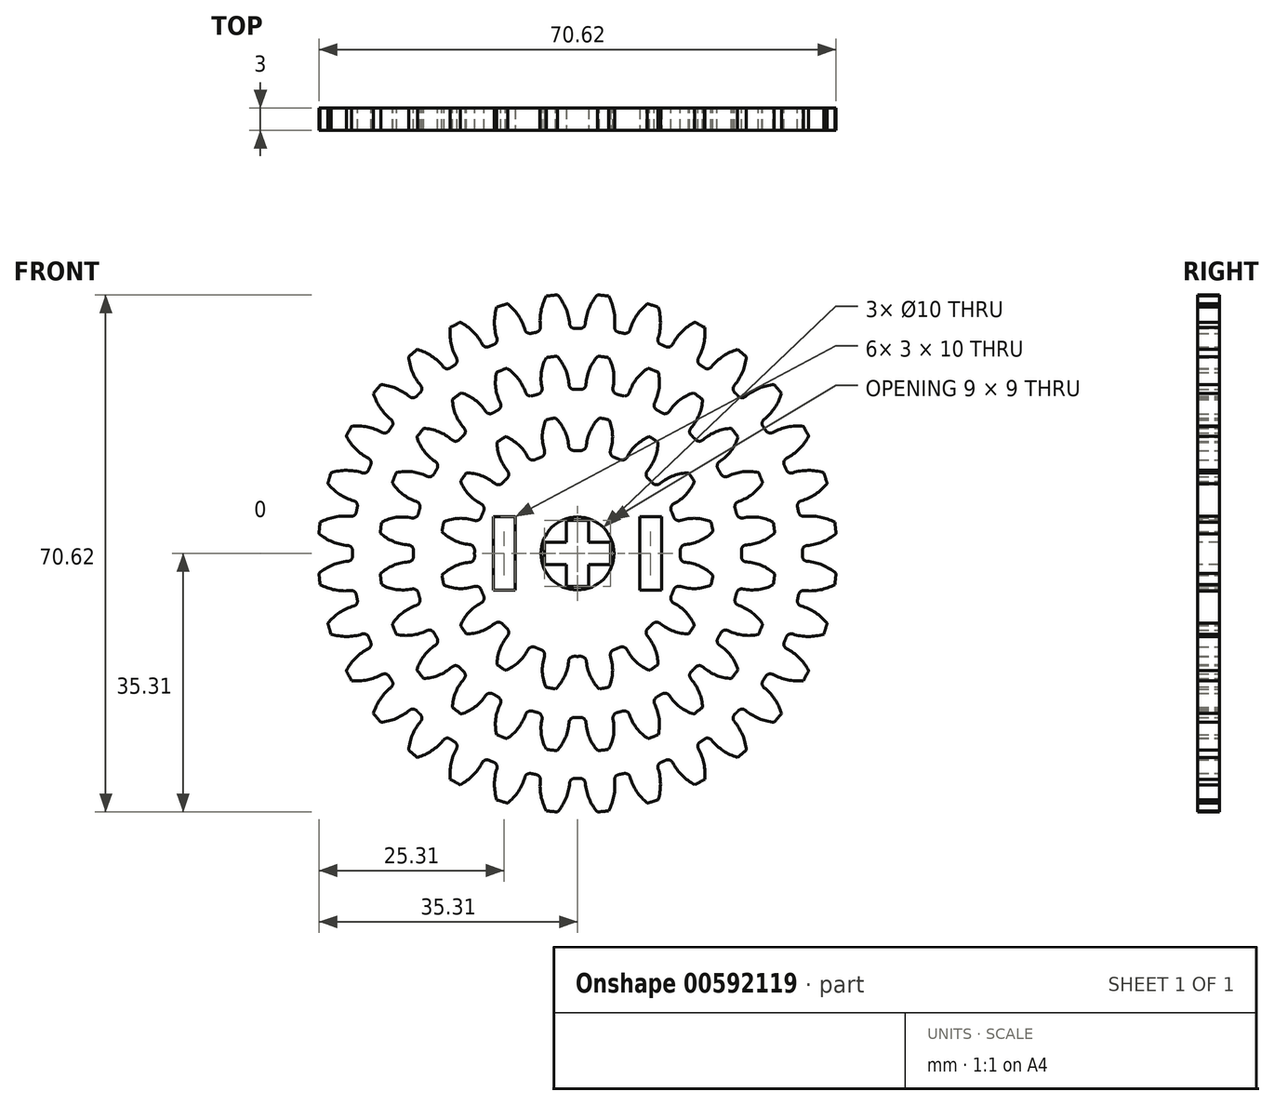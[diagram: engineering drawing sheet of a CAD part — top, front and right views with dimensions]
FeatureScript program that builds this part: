
annotation { "Feature Type Name" : "Feature", "Feature Type Description" : "" }
export const myFeature = defineFeature(function(context is Context, id is Id, definition is map)
    precondition{}
    {
        {
            var Q0;
            Q0=qCreatedBy(makeId("Front.planeOp"),FACE);
            var sketch = newSketch(context, id + "F0", { "sketchPlane" : qUnion([Q0])});
            skArc(sketch, "E0.0", {"start": v(4.27, 26.74) * mm, "mid": v(3.54, 26.85) * mm, "end": v(2.8, 26.94) * mm});
            skArc(sketch, "E1.0", {"start": v(5.4, 21.73) * mm, "mid": v(4.95, 22.07) * mm, "end": v(4.85, 22.62) * mm});
            skArc(sketch, "E2.0", {"start": v(6.18, 21.53) * mm, "mid": v(5.8, 21.63) * mm, "end": v(5.4, 21.73) * mm});
            skArc(sketch, "E3.0", {"start": v(7.1, 22.02) * mm, "mid": v(6.74, 21.58) * mm, "end": v(6.18, 21.53) * mm});
            skPoint(sketch, "E4.0", {"position": v(9.67, 25.3) * mm});
            skArc(sketch, "E5", {"start": v(4.85, 22.62) * mm, "mid": v(4.93, 24.74) * mm, "end": v(4.27, 26.74) * mm});
            skArc(sketch, "E6", {"start": v(7.1, 22.02) * mm, "mid": v(8.1, 23.89) * mm, "end": v(9.67, 25.3) * mm});
            skArc(sketch, "E7.1.0", {"start": v(11.54, 19.2) * mm, "mid": v(11.2, 19.4) * mm, "end": v(10.85, 19.6) * mm});
            skArc(sketch, "E7.1.1", {"start": v(10.85, 19.6) * mm, "mid": v(10.5, 20.03) * mm, "end": v(10.54, 20.6) * mm});
            skPoint(sketch, "E7.1.2", {"position": v(15.9, 21.93) * mm});
            skArc(sketch, "E7.1.3", {"start": v(12.56, 19.43) * mm, "mid": v(12.1, 19.1) * mm, "end": v(11.54, 19.2) * mm});
            skArc(sketch, "E7.1.4", {"start": v(12.56, 19.43) * mm, "mid": v(14, 20.98) * mm, "end": v(15.9, 21.93) * mm});
            skArc(sketch, "E7.1.5", {"start": v(10.54, 20.6) * mm, "mid": v(11.16, 22.62) * mm, "end": v(11.05, 24.73) * mm});
            skArc(sketch, "E7.1.6", {"start": v(11.05, 24.73) * mm, "mid": v(10.36, 25.02) * mm, "end": v(9.67, 25.3) * mm});
            skArc(sketch, "E7.2.0", {"start": v(16.12, 15.55) * mm, "mid": v(15.84, 15.84) * mm, "end": v(15.55, 16.12) * mm});
            skArc(sketch, "E7.2.1", {"start": v(15.55, 16.12) * mm, "mid": v(15.32, 16.63) * mm, "end": v(15.52, 17.16) * mm});
            skPoint(sketch, "E7.2.2", {"position": v(21.03, 17.07) * mm});
            skArc(sketch, "E7.2.3", {"start": v(17.16, 15.52) * mm, "mid": v(16.63, 15.32) * mm, "end": v(16.12, 15.55) * mm});
            skArc(sketch, "E7.2.4", {"start": v(17.16, 15.52) * mm, "mid": v(18.96, 16.64) * mm, "end": v(21.03, 17.07) * mm});
            skArc(sketch, "E7.2.5", {"start": v(15.52, 17.16) * mm, "mid": v(16.64, 18.96) * mm, "end": v(17.07, 21.03) * mm});
            skArc(sketch, "E7.2.6", {"start": v(17.07, 21.03) * mm, "mid": v(16.49, 21.49) * mm, "end": v(15.9, 21.93) * mm});
            skArc(sketch, "E7.3.0", {"start": v(19.6, 10.85) * mm, "mid": v(19.4, 11.2) * mm, "end": v(19.2, 11.54) * mm});
            skArc(sketch, "E7.3.1", {"start": v(19.2, 11.54) * mm, "mid": v(19.1, 12.1) * mm, "end": v(19.43, 12.56) * mm});
            skPoint(sketch, "E7.3.2", {"position": v(24.73, 11.05) * mm});
            skArc(sketch, "E7.3.3", {"start": v(20.6, 10.54) * mm, "mid": v(20.03, 10.5) * mm, "end": v(19.6, 10.85) * mm});
            skArc(sketch, "E7.3.4", {"start": v(20.6, 10.54) * mm, "mid": v(22.62, 11.16) * mm, "end": v(24.73, 11.05) * mm});
            skArc(sketch, "E7.3.5", {"start": v(19.43, 12.56) * mm, "mid": v(20.98, 14) * mm, "end": v(21.93, 15.9) * mm});
            skArc(sketch, "E7.3.6", {"start": v(21.93, 15.9) * mm, "mid": v(21.49, 16.49) * mm, "end": v(21.03, 17.07) * mm});
            skArc(sketch, "E7.4.0", {"start": v(21.73, 5.4) * mm, "mid": v(21.63, 5.8) * mm, "end": v(21.53, 6.18) * mm});
            skArc(sketch, "E7.4.1", {"start": v(21.53, 6.18) * mm, "mid": v(21.58, 6.74) * mm, "end": v(22.02, 7.1) * mm});
            skPoint(sketch, "E7.4.2", {"position": v(26.74, 4.27) * mm});
            skArc(sketch, "E7.4.3", {"start": v(22.62, 4.85) * mm, "mid": v(22.07, 4.95) * mm, "end": v(21.73, 5.4) * mm});
            skArc(sketch, "E7.4.4", {"start": v(22.62, 4.85) * mm, "mid": v(24.74, 4.93) * mm, "end": v(26.74, 4.27) * mm});
            skArc(sketch, "E7.4.5", {"start": v(22.02, 7.1) * mm, "mid": v(23.89, 8.1) * mm, "end": v(25.3, 9.67) * mm});
            skArc(sketch, "E7.4.6", {"start": v(25.3, 9.67) * mm, "mid": v(25.02, 10.36) * mm, "end": v(24.73, 11.05) * mm});
            skArc(sketch, "E7.5.0", {"start": v(22.4, -0.4) * mm, "mid": v(22.4, 0) * mm, "end": v(22.4, 0.4) * mm});
            skArc(sketch, "E7.5.1", {"start": v(22.4, 0.4) * mm, "mid": v(22.6, 0.93) * mm, "end": v(23.1, 1.17) * mm});
            skPoint(sketch, "E7.5.2", {"position": v(26.94, -2.8) * mm});
            skArc(sketch, "E7.5.3", {"start": v(23.1, -1.17) * mm, "mid": v(22.6, -0.93) * mm, "end": v(22.4, -0.4) * mm});
            skArc(sketch, "E7.5.4", {"start": v(23.1, -1.17) * mm, "mid": v(25.17, -1.64) * mm, "end": v(26.94, -2.8) * mm});
            skArc(sketch, "E7.5.5", {"start": v(23.1, 1.17) * mm, "mid": v(25.17, 1.64) * mm, "end": v(26.94, 2.8) * mm});
            skArc(sketch, "E7.5.6", {"start": v(26.94, 2.8) * mm, "mid": v(26.85, 3.54) * mm, "end": v(26.74, 4.27) * mm});
            skArc(sketch, "E7.6.0", {"start": v(21.53, -6.18) * mm, "mid": v(21.63, -5.8) * mm, "end": v(21.73, -5.4) * mm});
            skArc(sketch, "E7.6.1", {"start": v(21.73, -5.4) * mm, "mid": v(22.07, -4.95) * mm, "end": v(22.62, -4.85) * mm});
            skPoint(sketch, "E7.6.2", {"position": v(25.3, -9.67) * mm});
            skArc(sketch, "E7.6.3", {"start": v(22.02, -7.1) * mm, "mid": v(21.58, -6.74) * mm, "end": v(21.53, -6.18) * mm});
            skArc(sketch, "E7.6.4", {"start": v(22.02, -7.1) * mm, "mid": v(23.89, -8.1) * mm, "end": v(25.3, -9.67) * mm});
            skArc(sketch, "E7.6.5", {"start": v(22.62, -4.85) * mm, "mid": v(24.74, -4.93) * mm, "end": v(26.74, -4.27) * mm});
            skArc(sketch, "E7.6.6", {"start": v(26.74, -4.27) * mm, "mid": v(26.85, -3.54) * mm, "end": v(26.94, -2.8) * mm});
            skArc(sketch, "E7.7.0", {"start": v(19.2, -11.54) * mm, "mid": v(19.4, -11.2) * mm, "end": v(19.6, -10.85) * mm});
            skArc(sketch, "E7.7.1", {"start": v(19.6, -10.85) * mm, "mid": v(20.03, -10.5) * mm, "end": v(20.6, -10.54) * mm});
            skPoint(sketch, "E7.7.2", {"position": v(21.93, -15.9) * mm});
            skArc(sketch, "E7.7.3", {"start": v(19.43, -12.56) * mm, "mid": v(19.1, -12.1) * mm, "end": v(19.2, -11.54) * mm});
            skArc(sketch, "E7.7.4", {"start": v(19.43, -12.56) * mm, "mid": v(20.98, -14) * mm, "end": v(21.93, -15.9) * mm});
            skArc(sketch, "E7.7.5", {"start": v(20.6, -10.54) * mm, "mid": v(22.62, -11.16) * mm, "end": v(24.73, -11.05) * mm});
            skArc(sketch, "E7.7.6", {"start": v(24.73, -11.05) * mm, "mid": v(25.02, -10.36) * mm, "end": v(25.3, -9.67) * mm});
            skArc(sketch, "E7.8.0", {"start": v(15.55, -16.12) * mm, "mid": v(15.84, -15.84) * mm, "end": v(16.12, -15.55) * mm});
            skArc(sketch, "E7.8.1", {"start": v(16.12, -15.55) * mm, "mid": v(16.63, -15.32) * mm, "end": v(17.16, -15.52) * mm});
            skPoint(sketch, "E7.8.2", {"position": v(17.07, -21.03) * mm});
            skArc(sketch, "E7.8.3", {"start": v(15.52, -17.16) * mm, "mid": v(15.32, -16.63) * mm, "end": v(15.55, -16.12) * mm});
            skArc(sketch, "E7.8.4", {"start": v(15.52, -17.16) * mm, "mid": v(16.64, -18.96) * mm, "end": v(17.07, -21.03) * mm});
            skArc(sketch, "E7.8.5", {"start": v(17.16, -15.52) * mm, "mid": v(18.96, -16.64) * mm, "end": v(21.03, -17.07) * mm});
            skArc(sketch, "E7.8.6", {"start": v(21.03, -17.07) * mm, "mid": v(21.49, -16.49) * mm, "end": v(21.93, -15.9) * mm});
            skArc(sketch, "E7.9.0", {"start": v(10.85, -19.6) * mm, "mid": v(11.2, -19.4) * mm, "end": v(11.54, -19.2) * mm});
            skArc(sketch, "E7.9.1", {"start": v(11.54, -19.2) * mm, "mid": v(12.1, -19.1) * mm, "end": v(12.56, -19.43) * mm});
            skPoint(sketch, "E7.9.2", {"position": v(11.05, -24.73) * mm});
            skArc(sketch, "E7.9.3", {"start": v(10.54, -20.6) * mm, "mid": v(10.5, -20.03) * mm, "end": v(10.85, -19.6) * mm});
            skArc(sketch, "E7.9.4", {"start": v(10.54, -20.6) * mm, "mid": v(11.16, -22.62) * mm, "end": v(11.05, -24.73) * mm});
            skArc(sketch, "E7.9.5", {"start": v(12.56, -19.43) * mm, "mid": v(14, -20.98) * mm, "end": v(15.9, -21.93) * mm});
            skArc(sketch, "E7.9.6", {"start": v(15.9, -21.93) * mm, "mid": v(16.49, -21.49) * mm, "end": v(17.07, -21.03) * mm});
            skArc(sketch, "E7.10.0", {"start": v(5.4, -21.73) * mm, "mid": v(5.8, -21.63) * mm, "end": v(6.18, -21.53) * mm});
            skArc(sketch, "E7.10.1", {"start": v(6.18, -21.53) * mm, "mid": v(6.74, -21.58) * mm, "end": v(7.1, -22.02) * mm});
            skPoint(sketch, "E7.10.2", {"position": v(4.27, -26.74) * mm});
            skArc(sketch, "E7.10.3", {"start": v(4.85, -22.62) * mm, "mid": v(4.95, -22.07) * mm, "end": v(5.4, -21.73) * mm});
            skArc(sketch, "E7.10.4", {"start": v(4.85, -22.62) * mm, "mid": v(4.93, -24.74) * mm, "end": v(4.27, -26.74) * mm});
            skArc(sketch, "E7.10.5", {"start": v(7.1, -22.02) * mm, "mid": v(8.1, -23.89) * mm, "end": v(9.67, -25.3) * mm});
            skArc(sketch, "E7.10.6", {"start": v(9.67, -25.3) * mm, "mid": v(10.36, -25.02) * mm, "end": v(11.05, -24.73) * mm});
            skArc(sketch, "E7.11.0", {"start": v(-0.4, -22.4) * mm, "mid": v(0, -22.4) * mm, "end": v(0.4, -22.4) * mm});
            skArc(sketch, "E7.11.1", {"start": v(0.4, -22.4) * mm, "mid": v(0.93, -22.6) * mm, "end": v(1.17, -23.1) * mm});
            skPoint(sketch, "E7.11.2", {"position": v(-2.8, -26.94) * mm});
            skArc(sketch, "E7.11.3", {"start": v(-1.17, -23.1) * mm, "mid": v(-0.93, -22.6) * mm, "end": v(-0.4, -22.4) * mm});
            skArc(sketch, "E7.11.4", {"start": v(-1.17, -23.1) * mm, "mid": v(-1.64, -25.17) * mm, "end": v(-2.8, -26.94) * mm});
            skArc(sketch, "E7.11.5", {"start": v(1.17, -23.1) * mm, "mid": v(1.64, -25.17) * mm, "end": v(2.8, -26.94) * mm});
            skArc(sketch, "E7.11.6", {"start": v(2.8, -26.94) * mm, "mid": v(3.54, -26.85) * mm, "end": v(4.27, -26.74) * mm});
            skArc(sketch, "E7.12.0", {"start": v(-6.18, -21.53) * mm, "mid": v(-5.8, -21.63) * mm, "end": v(-5.4, -21.73) * mm});
            skArc(sketch, "E7.12.1", {"start": v(-5.4, -21.73) * mm, "mid": v(-4.95, -22.07) * mm, "end": v(-4.85, -22.62) * mm});
            skPoint(sketch, "E7.12.2", {"position": v(-9.67, -25.3) * mm});
            skArc(sketch, "E7.12.3", {"start": v(-7.1, -22.02) * mm, "mid": v(-6.74, -21.58) * mm, "end": v(-6.18, -21.53) * mm});
            skArc(sketch, "E7.12.4", {"start": v(-7.1, -22.02) * mm, "mid": v(-8.1, -23.89) * mm, "end": v(-9.67, -25.3) * mm});
            skArc(sketch, "E7.12.5", {"start": v(-4.85, -22.62) * mm, "mid": v(-4.93, -24.74) * mm, "end": v(-4.27, -26.74) * mm});
            skArc(sketch, "E7.12.6", {"start": v(-4.27, -26.74) * mm, "mid": v(-3.54, -26.85) * mm, "end": v(-2.8, -26.94) * mm});
            skArc(sketch, "E7.13.0", {"start": v(-11.54, -19.2) * mm, "mid": v(-11.2, -19.4) * mm, "end": v(-10.85, -19.6) * mm});
            skArc(sketch, "E7.13.1", {"start": v(-10.85, -19.6) * mm, "mid": v(-10.5, -20.03) * mm, "end": v(-10.54, -20.6) * mm});
            skPoint(sketch, "E7.13.2", {"position": v(-15.9, -21.93) * mm});
            skArc(sketch, "E7.13.3", {"start": v(-12.56, -19.43) * mm, "mid": v(-12.1, -19.1) * mm, "end": v(-11.54, -19.2) * mm});
            skArc(sketch, "E7.13.4", {"start": v(-12.56, -19.43) * mm, "mid": v(-14, -20.98) * mm, "end": v(-15.9, -21.93) * mm});
            skArc(sketch, "E7.13.5", {"start": v(-10.54, -20.6) * mm, "mid": v(-11.16, -22.62) * mm, "end": v(-11.05, -24.73) * mm});
            skArc(sketch, "E7.13.6", {"start": v(-11.05, -24.73) * mm, "mid": v(-10.36, -25.02) * mm, "end": v(-9.67, -25.3) * mm});
            skArc(sketch, "E7.14.0", {"start": v(-16.12, -15.55) * mm, "mid": v(-15.84, -15.84) * mm, "end": v(-15.55, -16.12) * mm});
            skArc(sketch, "E7.14.1", {"start": v(-15.55, -16.12) * mm, "mid": v(-15.32, -16.63) * mm, "end": v(-15.52, -17.16) * mm});
            skPoint(sketch, "E7.14.2", {"position": v(-21.03, -17.07) * mm});
            skArc(sketch, "E7.14.3", {"start": v(-17.16, -15.52) * mm, "mid": v(-16.63, -15.32) * mm, "end": v(-16.12, -15.55) * mm});
            skArc(sketch, "E7.14.4", {"start": v(-17.16, -15.52) * mm, "mid": v(-18.96, -16.64) * mm, "end": v(-21.03, -17.07) * mm});
            skArc(sketch, "E7.14.5", {"start": v(-15.52, -17.16) * mm, "mid": v(-16.64, -18.96) * mm, "end": v(-17.07, -21.03) * mm});
            skArc(sketch, "E7.14.6", {"start": v(-17.07, -21.03) * mm, "mid": v(-16.49, -21.49) * mm, "end": v(-15.9, -21.93) * mm});
            skArc(sketch, "E7.15.0", {"start": v(-19.6, -10.85) * mm, "mid": v(-19.4, -11.2) * mm, "end": v(-19.2, -11.54) * mm});
            skArc(sketch, "E7.15.1", {"start": v(-19.2, -11.54) * mm, "mid": v(-19.1, -12.1) * mm, "end": v(-19.43, -12.56) * mm});
            skPoint(sketch, "E7.15.2", {"position": v(-24.73, -11.05) * mm});
            skArc(sketch, "E7.15.3", {"start": v(-20.6, -10.54) * mm, "mid": v(-20.03, -10.5) * mm, "end": v(-19.6, -10.85) * mm});
            skArc(sketch, "E7.15.4", {"start": v(-20.6, -10.54) * mm, "mid": v(-22.62, -11.16) * mm, "end": v(-24.73, -11.05) * mm});
            skArc(sketch, "E7.15.5", {"start": v(-19.43, -12.56) * mm, "mid": v(-20.98, -14) * mm, "end": v(-21.93, -15.9) * mm});
            skArc(sketch, "E7.15.6", {"start": v(-21.93, -15.9) * mm, "mid": v(-21.49, -16.49) * mm, "end": v(-21.03, -17.07) * mm});
            skArc(sketch, "E7.16.0", {"start": v(-21.73, -5.4) * mm, "mid": v(-21.63, -5.8) * mm, "end": v(-21.53, -6.18) * mm});
            skArc(sketch, "E7.16.1", {"start": v(-21.53, -6.18) * mm, "mid": v(-21.58, -6.74) * mm, "end": v(-22.02, -7.1) * mm});
            skPoint(sketch, "E7.16.2", {"position": v(-26.74, -4.27) * mm});
            skArc(sketch, "E7.16.3", {"start": v(-22.62, -4.85) * mm, "mid": v(-22.07, -4.95) * mm, "end": v(-21.73, -5.4) * mm});
            skArc(sketch, "E7.16.4", {"start": v(-22.62, -4.85) * mm, "mid": v(-24.74, -4.93) * mm, "end": v(-26.74, -4.27) * mm});
            skArc(sketch, "E7.16.5", {"start": v(-22.02, -7.1) * mm, "mid": v(-23.89, -8.1) * mm, "end": v(-25.3, -9.67) * mm});
            skArc(sketch, "E7.16.6", {"start": v(-25.3, -9.67) * mm, "mid": v(-25.02, -10.36) * mm, "end": v(-24.73, -11.05) * mm});
            skArc(sketch, "E7.17.0", {"start": v(-22.4, 0.4) * mm, "mid": v(-22.4, 0) * mm, "end": v(-22.4, -0.4) * mm});
            skArc(sketch, "E7.17.1", {"start": v(-22.4, -0.4) * mm, "mid": v(-22.6, -0.93) * mm, "end": v(-23.1, -1.17) * mm});
            skPoint(sketch, "E7.17.2", {"position": v(-26.94, 2.8) * mm});
            skArc(sketch, "E7.17.3", {"start": v(-23.1, 1.17) * mm, "mid": v(-22.6, 0.93) * mm, "end": v(-22.4, 0.4) * mm});
            skArc(sketch, "E7.17.4", {"start": v(-23.1, 1.17) * mm, "mid": v(-25.17, 1.64) * mm, "end": v(-26.94, 2.8) * mm});
            skArc(sketch, "E7.17.5", {"start": v(-23.1, -1.17) * mm, "mid": v(-25.17, -1.64) * mm, "end": v(-26.94, -2.8) * mm});
            skArc(sketch, "E7.17.6", {"start": v(-26.94, -2.8) * mm, "mid": v(-26.85, -3.54) * mm, "end": v(-26.74, -4.27) * mm});
            skArc(sketch, "E7.18.0", {"start": v(-21.53, 6.18) * mm, "mid": v(-21.63, 5.8) * mm, "end": v(-21.73, 5.4) * mm});
            skArc(sketch, "E7.18.1", {"start": v(-21.73, 5.4) * mm, "mid": v(-22.07, 4.95) * mm, "end": v(-22.62, 4.85) * mm});
            skPoint(sketch, "E7.18.2", {"position": v(-25.3, 9.67) * mm});
            skArc(sketch, "E7.18.3", {"start": v(-22.02, 7.1) * mm, "mid": v(-21.58, 6.74) * mm, "end": v(-21.53, 6.18) * mm});
            skArc(sketch, "E7.18.4", {"start": v(-22.02, 7.1) * mm, "mid": v(-23.89, 8.1) * mm, "end": v(-25.3, 9.67) * mm});
            skArc(sketch, "E7.18.5", {"start": v(-22.62, 4.85) * mm, "mid": v(-24.74, 4.93) * mm, "end": v(-26.74, 4.27) * mm});
            skArc(sketch, "E7.18.6", {"start": v(-26.74, 4.27) * mm, "mid": v(-26.85, 3.54) * mm, "end": v(-26.94, 2.8) * mm});
            skArc(sketch, "E7.19.0", {"start": v(-19.2, 11.54) * mm, "mid": v(-19.4, 11.2) * mm, "end": v(-19.6, 10.85) * mm});
            skArc(sketch, "E7.19.1", {"start": v(-19.6, 10.85) * mm, "mid": v(-20.03, 10.5) * mm, "end": v(-20.6, 10.54) * mm});
            skPoint(sketch, "E7.19.2", {"position": v(-21.93, 15.9) * mm});
            skArc(sketch, "E7.19.3", {"start": v(-19.43, 12.56) * mm, "mid": v(-19.1, 12.1) * mm, "end": v(-19.2, 11.54) * mm});
            skArc(sketch, "E7.19.4", {"start": v(-19.43, 12.56) * mm, "mid": v(-20.98, 14) * mm, "end": v(-21.93, 15.9) * mm});
            skArc(sketch, "E7.19.5", {"start": v(-20.6, 10.54) * mm, "mid": v(-22.62, 11.16) * mm, "end": v(-24.73, 11.05) * mm});
            skArc(sketch, "E7.19.6", {"start": v(-24.73, 11.05) * mm, "mid": v(-25.02, 10.36) * mm, "end": v(-25.3, 9.67) * mm});
            skArc(sketch, "E7.20.0", {"start": v(-15.55, 16.12) * mm, "mid": v(-15.84, 15.84) * mm, "end": v(-16.12, 15.55) * mm});
            skArc(sketch, "E7.20.1", {"start": v(-16.12, 15.55) * mm, "mid": v(-16.63, 15.32) * mm, "end": v(-17.16, 15.52) * mm});
            skPoint(sketch, "E7.20.2", {"position": v(-17.07, 21.03) * mm});
            skArc(sketch, "E7.20.3", {"start": v(-15.52, 17.16) * mm, "mid": v(-15.32, 16.63) * mm, "end": v(-15.55, 16.12) * mm});
            skArc(sketch, "E7.20.4", {"start": v(-15.52, 17.16) * mm, "mid": v(-16.64, 18.96) * mm, "end": v(-17.07, 21.03) * mm});
            skArc(sketch, "E7.20.5", {"start": v(-17.16, 15.52) * mm, "mid": v(-18.96, 16.64) * mm, "end": v(-21.03, 17.07) * mm});
            skArc(sketch, "E7.20.6", {"start": v(-21.03, 17.07) * mm, "mid": v(-21.49, 16.49) * mm, "end": v(-21.93, 15.9) * mm});
            skArc(sketch, "E7.21.0", {"start": v(-10.85, 19.6) * mm, "mid": v(-11.2, 19.4) * mm, "end": v(-11.54, 19.2) * mm});
            skArc(sketch, "E7.21.1", {"start": v(-11.54, 19.2) * mm, "mid": v(-12.1, 19.1) * mm, "end": v(-12.56, 19.43) * mm});
            skPoint(sketch, "E7.21.2", {"position": v(-11.05, 24.73) * mm});
            skArc(sketch, "E7.21.3", {"start": v(-10.54, 20.6) * mm, "mid": v(-10.5, 20.03) * mm, "end": v(-10.85, 19.6) * mm});
            skArc(sketch, "E7.21.4", {"start": v(-10.54, 20.6) * mm, "mid": v(-11.16, 22.62) * mm, "end": v(-11.05, 24.73) * mm});
            skArc(sketch, "E7.21.5", {"start": v(-12.56, 19.43) * mm, "mid": v(-14, 20.98) * mm, "end": v(-15.9, 21.93) * mm});
            skArc(sketch, "E7.21.6", {"start": v(-15.9, 21.93) * mm, "mid": v(-16.49, 21.49) * mm, "end": v(-17.07, 21.03) * mm});
            skArc(sketch, "E7.22.0", {"start": v(-5.4, 21.73) * mm, "mid": v(-5.8, 21.63) * mm, "end": v(-6.18, 21.53) * mm});
            skArc(sketch, "E7.22.1", {"start": v(-6.18, 21.53) * mm, "mid": v(-6.74, 21.58) * mm, "end": v(-7.1, 22.02) * mm});
            skPoint(sketch, "E7.22.2", {"position": v(-4.27, 26.74) * mm});
            skArc(sketch, "E7.22.3", {"start": v(-4.85, 22.62) * mm, "mid": v(-4.95, 22.07) * mm, "end": v(-5.4, 21.73) * mm});
            skArc(sketch, "E7.22.4", {"start": v(-4.85, 22.62) * mm, "mid": v(-4.93, 24.74) * mm, "end": v(-4.27, 26.74) * mm});
            skArc(sketch, "E7.22.5", {"start": v(-7.1, 22.02) * mm, "mid": v(-8.1, 23.89) * mm, "end": v(-9.67, 25.3) * mm});
            skArc(sketch, "E7.22.6", {"start": v(-9.67, 25.3) * mm, "mid": v(-10.36, 25.02) * mm, "end": v(-11.05, 24.73) * mm});
            skArc(sketch, "E7.23.0", {"start": v(0.4, 22.4) * mm, "mid": v(0, 22.4) * mm, "end": v(-0.4, 22.4) * mm});
            skArc(sketch, "E7.23.1", {"start": v(-0.4, 22.4) * mm, "mid": v(-0.93, 22.6) * mm, "end": v(-1.17, 23.1) * mm});
            skPoint(sketch, "E7.23.2", {"position": v(2.8, 26.94) * mm});
            skArc(sketch, "E7.23.3", {"start": v(1.17, 23.1) * mm, "mid": v(0.93, 22.6) * mm, "end": v(0.4, 22.4) * mm});
            skArc(sketch, "E7.23.4", {"start": v(1.17, 23.1) * mm, "mid": v(1.64, 25.17) * mm, "end": v(2.8, 26.94) * mm});
            skArc(sketch, "E7.23.5", {"start": v(-1.17, 23.1) * mm, "mid": v(-1.64, 25.17) * mm, "end": v(-2.8, 26.94) * mm});
            skArc(sketch, "E7.23.6", {"start": v(-2.8, 26.94) * mm, "mid": v(-3.54, 26.85) * mm, "end": v(-4.27, 26.74) * mm});
            skLineSegment(sketch, "E7.anchor1", {"start": v(0, 0) * mm, "end": v(-1.06, 23.89) * mm, "construction": true});
            skLineSegment(sketch, "E7.anchor2", {"start": v(0, 0) * mm, "end": v(-7.2, 22.8) * mm, "construction": true});
            skLineSegment(sketch, "E8.bottom", {"start": v(1.38, 1.37) * mm, "end": v(-1.37, 1.37) * mm});
            skLineSegment(sketch, "E8.top", {"start": v(1.37, -1.38) * mm, "end": v(-1.37, -1.38) * mm});
            skLineSegment(sketch, "E8.left", {"start": v(1.37, 1.37) * mm, "end": v(1.37, -1.38) * mm});
            skLineSegment(sketch, "E8.right", {"start": v(-1.37, 1.38) * mm, "end": v(-1.37, -1.37) * mm});
            skSolve(sketch);
        }
        {
            var Q0;
            Q0=makeQuery(id+"F0.imprint","IMPRINT",FACE,{"disambiguationData":[TD([[makeQuery(id+"F0.imprint","IMPRINT",EDGE,{"derivedFrom":sQuery(id+"F0.wireOp",EDGE,"E0.0")}),1.0]])]});
            extrude(context, id + "F1", {"entities" : qUnion([Q0]), "depth" : 3 * mm, "offsetDistance" : 25 * mm});
        }
        {
            var Q0;
            Q0=qCreatedBy(makeId("Front.planeOp"),FACE);
            var sketch = newSketch(context, id + "F2", { "sketchPlane" : qUnion([Q0])});
            skArc(sketch, "E9.0", {"start": v(4.33, 18.24) * mm, "mid": v(3.66, 18.39) * mm, "end": v(2.98, 18.51) * mm});
            skArc(sketch, "E10.0", {"start": v(4.98, 13.15) * mm, "mid": v(4.56, 13.54) * mm, "end": v(4.52, 14.12) * mm});
            skArc(sketch, "E11.0", {"start": v(5.78, 12.82) * mm, "mid": v(5.38, 13) * mm, "end": v(4.98, 13.15) * mm});
            skArc(sketch, "E12.0", {"start": v(6.79, 13.18) * mm, "mid": v(6.35, 12.8) * mm, "end": v(5.78, 12.82) * mm});
            skPoint(sketch, "E13.0", {"position": v(9.83, 15.96) * mm});
            skArc(sketch, "E14", {"start": v(4.52, 14.12) * mm, "mid": v(4.8, 16.2) * mm, "end": v(4.33, 18.24) * mm});
            skArc(sketch, "E15", {"start": v(6.79, 13.18) * mm, "mid": v(8.06, 14.84) * mm, "end": v(9.83, 15.96) * mm});
            skArc(sketch, "E16.1.0", {"start": v(11.31, 9.57) * mm, "mid": v(10.77, 9.4) * mm, "end": v(10.24, 9.63) * mm});
            skArc(sketch, "E16.1.1", {"start": v(10.24, 9.63) * mm, "mid": v(9.94, 9.94) * mm, "end": v(9.63, 10.24) * mm});
            skArc(sketch, "E16.1.2", {"start": v(9.57, 11.31) * mm, "mid": v(10.63, 13.13) * mm, "end": v(10.98, 15.2) * mm});
            skArc(sketch, "E16.1.3", {"start": v(11.31, 9.57) * mm, "mid": v(13.13, 10.63) * mm, "end": v(15.2, 10.98) * mm});
            skArc(sketch, "E16.1.4", {"start": v(10.98, 15.2) * mm, "mid": v(10.42, 15.59) * mm, "end": v(9.83, 15.96) * mm});
            skArc(sketch, "E16.1.5", {"start": v(9.63, 10.24) * mm, "mid": v(9.4, 10.77) * mm, "end": v(9.57, 11.31) * mm});
            skPoint(sketch, "E16.1.6", {"position": v(15.2, 10.98) * mm});
            skArc(sketch, "E16.2.0", {"start": v(14.12, 4.52) * mm, "mid": v(13.54, 4.56) * mm, "end": v(13.15, 4.98) * mm});
            skArc(sketch, "E16.2.1", {"start": v(13.15, 4.98) * mm, "mid": v(13, 5.38) * mm, "end": v(12.82, 5.78) * mm});
            skArc(sketch, "E16.2.2", {"start": v(13.18, 6.79) * mm, "mid": v(14.84, 8.06) * mm, "end": v(15.96, 9.83) * mm});
            skArc(sketch, "E16.2.3", {"start": v(14.12, 4.52) * mm, "mid": v(16.2, 4.8) * mm, "end": v(18.24, 4.33) * mm});
            skArc(sketch, "E16.2.4", {"start": v(15.96, 9.83) * mm, "mid": v(15.59, 10.42) * mm, "end": v(15.2, 10.98) * mm});
            skArc(sketch, "E16.2.5", {"start": v(12.82, 5.78) * mm, "mid": v(12.8, 6.35) * mm, "end": v(13.18, 6.79) * mm});
            skPoint(sketch, "E16.2.6", {"position": v(18.24, 4.33) * mm});
            skArc(sketch, "E16.3.0", {"start": v(14.77, -1.23) * mm, "mid": v(14.25, -0.97) * mm, "end": v(14.05, -0.43) * mm});
            skArc(sketch, "E16.3.1", {"start": v(14.05, -0.43) * mm, "mid": v(14.06, 0) * mm, "end": v(14.05, 0.43) * mm});
            skArc(sketch, "E16.3.2", {"start": v(14.77, 1.23) * mm, "mid": v(16.8, 1.77) * mm, "end": v(18.51, 2.98) * mm});
            skArc(sketch, "E16.3.3", {"start": v(14.77, -1.23) * mm, "mid": v(16.8, -1.77) * mm, "end": v(18.51, -2.98) * mm});
            skArc(sketch, "E16.3.4", {"start": v(18.51, 2.98) * mm, "mid": v(18.39, 3.66) * mm, "end": v(18.24, 4.33) * mm});
            skArc(sketch, "E16.3.5", {"start": v(14.05, 0.43) * mm, "mid": v(14.25, 0.97) * mm, "end": v(14.77, 1.23) * mm});
            skPoint(sketch, "E16.3.6", {"position": v(18.51, -2.98) * mm});
            skArc(sketch, "E16.4.0", {"start": v(13.18, -6.79) * mm, "mid": v(12.8, -6.35) * mm, "end": v(12.82, -5.78) * mm});
            skArc(sketch, "E16.4.1", {"start": v(12.82, -5.78) * mm, "mid": v(13, -5.38) * mm, "end": v(13.15, -4.98) * mm});
            skArc(sketch, "E16.4.2", {"start": v(14.12, -4.52) * mm, "mid": v(16.2, -4.8) * mm, "end": v(18.24, -4.33) * mm});
            skArc(sketch, "E16.4.3", {"start": v(13.18, -6.79) * mm, "mid": v(14.84, -8.06) * mm, "end": v(15.96, -9.83) * mm});
            skArc(sketch, "E16.4.4", {"start": v(18.24, -4.33) * mm, "mid": v(18.39, -3.66) * mm, "end": v(18.51, -2.98) * mm});
            skArc(sketch, "E16.4.5", {"start": v(13.15, -4.98) * mm, "mid": v(13.54, -4.56) * mm, "end": v(14.12, -4.52) * mm});
            skPoint(sketch, "E16.4.6", {"position": v(15.96, -9.83) * mm});
            skArc(sketch, "E16.5.0", {"start": v(9.57, -11.31) * mm, "mid": v(9.4, -10.77) * mm, "end": v(9.63, -10.24) * mm});
            skArc(sketch, "E16.5.1", {"start": v(9.63, -10.24) * mm, "mid": v(9.94, -9.94) * mm, "end": v(10.24, -9.63) * mm});
            skArc(sketch, "E16.5.2", {"start": v(11.31, -9.57) * mm, "mid": v(13.13, -10.63) * mm, "end": v(15.2, -10.98) * mm});
            skArc(sketch, "E16.5.3", {"start": v(9.57, -11.31) * mm, "mid": v(10.63, -13.13) * mm, "end": v(10.98, -15.2) * mm});
            skArc(sketch, "E16.5.4", {"start": v(15.2, -10.98) * mm, "mid": v(15.59, -10.42) * mm, "end": v(15.96, -9.83) * mm});
            skArc(sketch, "E16.5.5", {"start": v(10.24, -9.63) * mm, "mid": v(10.77, -9.4) * mm, "end": v(11.31, -9.57) * mm});
            skPoint(sketch, "E16.5.6", {"position": v(10.98, -15.2) * mm});
            skArc(sketch, "E16.6.0", {"start": v(4.52, -14.12) * mm, "mid": v(4.56, -13.54) * mm, "end": v(4.98, -13.15) * mm});
            skArc(sketch, "E16.6.1", {"start": v(4.98, -13.15) * mm, "mid": v(5.38, -13) * mm, "end": v(5.78, -12.82) * mm});
            skArc(sketch, "E16.6.2", {"start": v(6.79, -13.18) * mm, "mid": v(8.06, -14.84) * mm, "end": v(9.83, -15.96) * mm});
            skArc(sketch, "E16.6.3", {"start": v(4.52, -14.12) * mm, "mid": v(4.8, -16.2) * mm, "end": v(4.33, -18.24) * mm});
            skArc(sketch, "E16.6.4", {"start": v(9.83, -15.96) * mm, "mid": v(10.42, -15.59) * mm, "end": v(10.98, -15.2) * mm});
            skArc(sketch, "E16.6.5", {"start": v(5.78, -12.82) * mm, "mid": v(6.35, -12.8) * mm, "end": v(6.79, -13.18) * mm});
            skPoint(sketch, "E16.6.6", {"position": v(4.33, -18.24) * mm});
            skArc(sketch, "E16.7.0", {"start": v(-1.23, -14.77) * mm, "mid": v(-0.97, -14.25) * mm, "end": v(-0.43, -14.05) * mm});
            skArc(sketch, "E16.7.1", {"start": v(-0.43, -14.05) * mm, "mid": v(0, -14.06) * mm, "end": v(0.43, -14.05) * mm});
            skArc(sketch, "E16.7.2", {"start": v(1.23, -14.77) * mm, "mid": v(1.77, -16.8) * mm, "end": v(2.98, -18.51) * mm});
            skArc(sketch, "E16.7.3", {"start": v(-1.23, -14.77) * mm, "mid": v(-1.77, -16.8) * mm, "end": v(-2.98, -18.51) * mm});
            skArc(sketch, "E16.7.4", {"start": v(2.98, -18.51) * mm, "mid": v(3.66, -18.39) * mm, "end": v(4.33, -18.24) * mm});
            skArc(sketch, "E16.7.5", {"start": v(0.43, -14.05) * mm, "mid": v(0.97, -14.25) * mm, "end": v(1.23, -14.77) * mm});
            skPoint(sketch, "E16.7.6", {"position": v(-2.98, -18.51) * mm});
            skArc(sketch, "E16.8.0", {"start": v(-6.79, -13.18) * mm, "mid": v(-6.35, -12.8) * mm, "end": v(-5.78, -12.82) * mm});
            skArc(sketch, "E16.8.1", {"start": v(-5.78, -12.82) * mm, "mid": v(-5.38, -13) * mm, "end": v(-4.98, -13.15) * mm});
            skArc(sketch, "E16.8.2", {"start": v(-4.52, -14.12) * mm, "mid": v(-4.8, -16.2) * mm, "end": v(-4.33, -18.24) * mm});
            skArc(sketch, "E16.8.3", {"start": v(-6.79, -13.18) * mm, "mid": v(-8.06, -14.84) * mm, "end": v(-9.83, -15.96) * mm});
            skArc(sketch, "E16.8.4", {"start": v(-4.33, -18.24) * mm, "mid": v(-3.66, -18.39) * mm, "end": v(-2.98, -18.51) * mm});
            skArc(sketch, "E16.8.5", {"start": v(-4.98, -13.15) * mm, "mid": v(-4.56, -13.54) * mm, "end": v(-4.52, -14.12) * mm});
            skPoint(sketch, "E16.8.6", {"position": v(-9.83, -15.96) * mm});
            skArc(sketch, "E16.9.0", {"start": v(-11.31, -9.57) * mm, "mid": v(-10.77, -9.4) * mm, "end": v(-10.24, -9.63) * mm});
            skArc(sketch, "E16.9.1", {"start": v(-10.24, -9.63) * mm, "mid": v(-9.94, -9.94) * mm, "end": v(-9.63, -10.24) * mm});
            skArc(sketch, "E16.9.2", {"start": v(-9.57, -11.31) * mm, "mid": v(-10.63, -13.13) * mm, "end": v(-10.98, -15.2) * mm});
            skArc(sketch, "E16.9.3", {"start": v(-11.31, -9.57) * mm, "mid": v(-13.13, -10.63) * mm, "end": v(-15.2, -10.98) * mm});
            skArc(sketch, "E16.9.4", {"start": v(-10.98, -15.2) * mm, "mid": v(-10.42, -15.59) * mm, "end": v(-9.83, -15.96) * mm});
            skArc(sketch, "E16.9.5", {"start": v(-9.63, -10.24) * mm, "mid": v(-9.4, -10.77) * mm, "end": v(-9.57, -11.31) * mm});
            skPoint(sketch, "E16.9.6", {"position": v(-15.2, -10.98) * mm});
            skArc(sketch, "E16.10.0", {"start": v(-14.12, -4.52) * mm, "mid": v(-13.54, -4.56) * mm, "end": v(-13.15, -4.98) * mm});
            skArc(sketch, "E16.10.1", {"start": v(-13.15, -4.98) * mm, "mid": v(-13, -5.38) * mm, "end": v(-12.82, -5.78) * mm});
            skArc(sketch, "E16.10.2", {"start": v(-13.18, -6.79) * mm, "mid": v(-14.84, -8.06) * mm, "end": v(-15.96, -9.83) * mm});
            skArc(sketch, "E16.10.3", {"start": v(-14.12, -4.52) * mm, "mid": v(-16.2, -4.8) * mm, "end": v(-18.24, -4.33) * mm});
            skArc(sketch, "E16.10.4", {"start": v(-15.96, -9.83) * mm, "mid": v(-15.59, -10.42) * mm, "end": v(-15.2, -10.98) * mm});
            skArc(sketch, "E16.10.5", {"start": v(-12.82, -5.78) * mm, "mid": v(-12.8, -6.35) * mm, "end": v(-13.18, -6.79) * mm});
            skPoint(sketch, "E16.10.6", {"position": v(-18.24, -4.33) * mm});
            skArc(sketch, "E16.11.0", {"start": v(-14.77, 1.23) * mm, "mid": v(-14.25, 0.97) * mm, "end": v(-14.05, 0.43) * mm});
            skArc(sketch, "E16.11.1", {"start": v(-14.05, 0.43) * mm, "mid": v(-14.06, 0) * mm, "end": v(-14.05, -0.43) * mm});
            skArc(sketch, "E16.11.2", {"start": v(-14.77, -1.23) * mm, "mid": v(-16.8, -1.77) * mm, "end": v(-18.51, -2.98) * mm});
            skArc(sketch, "E16.11.3", {"start": v(-14.77, 1.23) * mm, "mid": v(-16.8, 1.77) * mm, "end": v(-18.51, 2.98) * mm});
            skArc(sketch, "E16.11.4", {"start": v(-18.51, -2.98) * mm, "mid": v(-18.39, -3.66) * mm, "end": v(-18.24, -4.33) * mm});
            skArc(sketch, "E16.11.5", {"start": v(-14.05, -0.43) * mm, "mid": v(-14.25, -0.97) * mm, "end": v(-14.77, -1.23) * mm});
            skPoint(sketch, "E16.11.6", {"position": v(-18.51, 2.98) * mm});
            skArc(sketch, "E16.12.0", {"start": v(-13.18, 6.79) * mm, "mid": v(-12.8, 6.35) * mm, "end": v(-12.82, 5.78) * mm});
            skArc(sketch, "E16.12.1", {"start": v(-12.82, 5.78) * mm, "mid": v(-13, 5.38) * mm, "end": v(-13.15, 4.98) * mm});
            skArc(sketch, "E16.12.2", {"start": v(-14.12, 4.52) * mm, "mid": v(-16.2, 4.8) * mm, "end": v(-18.24, 4.33) * mm});
            skArc(sketch, "E16.12.3", {"start": v(-13.18, 6.79) * mm, "mid": v(-14.84, 8.06) * mm, "end": v(-15.96, 9.83) * mm});
            skArc(sketch, "E16.12.4", {"start": v(-18.24, 4.33) * mm, "mid": v(-18.39, 3.66) * mm, "end": v(-18.51, 2.98) * mm});
            skArc(sketch, "E16.12.5", {"start": v(-13.15, 4.98) * mm, "mid": v(-13.54, 4.56) * mm, "end": v(-14.12, 4.52) * mm});
            skPoint(sketch, "E16.12.6", {"position": v(-15.96, 9.83) * mm});
            skArc(sketch, "E16.13.0", {"start": v(-9.57, 11.31) * mm, "mid": v(-9.4, 10.77) * mm, "end": v(-9.63, 10.24) * mm});
            skArc(sketch, "E16.13.1", {"start": v(-9.63, 10.24) * mm, "mid": v(-9.94, 9.94) * mm, "end": v(-10.24, 9.63) * mm});
            skArc(sketch, "E16.13.2", {"start": v(-11.31, 9.57) * mm, "mid": v(-13.13, 10.63) * mm, "end": v(-15.2, 10.98) * mm});
            skArc(sketch, "E16.13.3", {"start": v(-9.57, 11.31) * mm, "mid": v(-10.63, 13.13) * mm, "end": v(-10.98, 15.2) * mm});
            skArc(sketch, "E16.13.4", {"start": v(-15.2, 10.98) * mm, "mid": v(-15.59, 10.42) * mm, "end": v(-15.96, 9.83) * mm});
            skArc(sketch, "E16.13.5", {"start": v(-10.24, 9.63) * mm, "mid": v(-10.77, 9.4) * mm, "end": v(-11.31, 9.57) * mm});
            skPoint(sketch, "E16.13.6", {"position": v(-10.98, 15.2) * mm});
            skArc(sketch, "E16.14.0", {"start": v(-4.52, 14.12) * mm, "mid": v(-4.56, 13.54) * mm, "end": v(-4.98, 13.15) * mm});
            skArc(sketch, "E16.14.1", {"start": v(-4.98, 13.15) * mm, "mid": v(-5.38, 13) * mm, "end": v(-5.78, 12.82) * mm});
            skArc(sketch, "E16.14.2", {"start": v(-6.79, 13.18) * mm, "mid": v(-8.06, 14.84) * mm, "end": v(-9.83, 15.96) * mm});
            skArc(sketch, "E16.14.3", {"start": v(-4.52, 14.12) * mm, "mid": v(-4.8, 16.2) * mm, "end": v(-4.33, 18.24) * mm});
            skArc(sketch, "E16.14.4", {"start": v(-9.83, 15.96) * mm, "mid": v(-10.42, 15.59) * mm, "end": v(-10.98, 15.2) * mm});
            skArc(sketch, "E16.14.5", {"start": v(-5.78, 12.82) * mm, "mid": v(-6.35, 12.8) * mm, "end": v(-6.79, 13.18) * mm});
            skPoint(sketch, "E16.14.6", {"position": v(-4.33, 18.24) * mm});
            skArc(sketch, "E16.15.0", {"start": v(1.23, 14.77) * mm, "mid": v(0.97, 14.25) * mm, "end": v(0.43, 14.05) * mm});
            skArc(sketch, "E16.15.1", {"start": v(0.43, 14.05) * mm, "mid": v(0, 14.06) * mm, "end": v(-0.43, 14.05) * mm});
            skArc(sketch, "E16.15.2", {"start": v(-1.23, 14.77) * mm, "mid": v(-1.77, 16.8) * mm, "end": v(-2.98, 18.51) * mm});
            skArc(sketch, "E16.15.3", {"start": v(1.23, 14.77) * mm, "mid": v(1.77, 16.8) * mm, "end": v(2.98, 18.51) * mm});
            skArc(sketch, "E16.15.4", {"start": v(-2.98, 18.51) * mm, "mid": v(-3.66, 18.39) * mm, "end": v(-4.33, 18.24) * mm});
            skArc(sketch, "E16.15.5", {"start": v(-0.43, 14.05) * mm, "mid": v(-0.97, 14.25) * mm, "end": v(-1.23, 14.77) * mm});
            skPoint(sketch, "E16.15.6", {"position": v(2.98, 18.51) * mm});
            skLineSegment(sketch, "E16.anchor1", {"start": v(0, 0) * mm, "end": v(-1.13, 15.93) * mm, "construction": true});
            skLineSegment(sketch, "E16.anchor2", {"start": v(0, 0) * mm, "end": v(-7.14, 14.3) * mm, "construction": true});
            skLineSegment(sketch, "E17.bottom", {"start": v(1.38, 1.37) * mm, "end": v(-1.37, 1.38) * mm});
            skLineSegment(sketch, "E17.top", {"start": v(1.37, -1.38) * mm, "end": v(-1.38, -1.38) * mm});
            skLineSegment(sketch, "E17.left", {"start": v(1.38, 1.37) * mm, "end": v(1.37, -1.38) * mm});
            skLineSegment(sketch, "E17.right", {"start": v(-1.37, 1.38) * mm, "end": v(-1.37, -1.37) * mm});
            skSolve(sketch);
        }
        {
            var Q0;
            {var subQ101=sQuery(id+"F2.wireOp",EDGE,"E9.0");Q0=makeQuery(id+"F2.imprint","IMPRINT",FACE,{"disambiguationData":[TD([[makeQuery(id+"F2.imprint","IMPRINT",EDGE,{"derivedFrom":subQ101}),1.0]])]});}
            extrude(context, id + "F3", {"entities" : qUnion([Q0]), "depth" : 3 * mm, "offsetDistance" : 25 * mm});
        }
        {
            var Q0;
            Q0=qCreatedBy(makeId("Front.planeOp"),FACE);
            var sketch = newSketch(context, id + "F4", { "sketchPlane" : qUnion([Q0])});
            skArc(sketch, "E18.0", {"start": v(4.24, 35.16) * mm, "mid": v(3.47, 35.24) * mm, "end": v(2.7, 35.3) * mm});
            skArc(sketch, "E19.0", {"start": v(5.63, 30.2) * mm, "mid": v(5.2, 30.48) * mm, "end": v(5.06, 30.97) * mm});
            skArc(sketch, "E20.0", {"start": v(6.36, 30.06) * mm, "mid": v(6, 30.14) * mm, "end": v(5.63, 30.2) * mm});
            skArc(sketch, "E21.0", {"start": v(7.17, 30.55) * mm, "mid": v(6.86, 30.15) * mm, "end": v(6.36, 30.06) * mm});
            skPoint(sketch, "E22.0", {"position": v(9.54, 34.1) * mm});
            skArc(sketch, "E23", {"start": v(5.06, 30.97) * mm, "mid": v(4.98, 33.13) * mm, "end": v(4.24, 35.16) * mm});
            skArc(sketch, "E24", {"start": v(7.17, 30.55) * mm, "mid": v(8.08, 32.51) * mm, "end": v(9.54, 34.1) * mm});
            skArc(sketch, "E25.1.0", {"start": v(13, 28.57) * mm, "mid": v(14.27, 30.31) * mm, "end": v(16, 31.59) * mm});
            skArc(sketch, "E25.1.1", {"start": v(11, 29.39) * mm, "mid": v(11.34, 31.52) * mm, "end": v(11.02, 33.66) * mm});
            skPoint(sketch, "E25.1.2", {"position": v(16, 31.59) * mm});
            skArc(sketch, "E25.1.3", {"start": v(13, 28.57) * mm, "mid": v(12.61, 28.23) * mm, "end": v(12.1, 28.24) * mm});
            skArc(sketch, "E25.1.4", {"start": v(11.02, 33.66) * mm, "mid": v(10.28, 33.89) * mm, "end": v(9.54, 34.1) * mm});
            skArc(sketch, "E25.1.5", {"start": v(11.42, 28.53) * mm, "mid": v(11.04, 28.88) * mm, "end": v(11, 29.39) * mm});
            skArc(sketch, "E25.1.6", {"start": v(12.1, 28.24) * mm, "mid": v(11.76, 28.39) * mm, "end": v(11.42, 28.53) * mm});
            skArc(sketch, "E25.2.0", {"start": v(18.32, 25.48) * mm, "mid": v(19.9, 26.94) * mm, "end": v(21.86, 27.86) * mm});
            skArc(sketch, "E25.2.1", {"start": v(16.53, 26.68) * mm, "mid": v(17.28, 28.7) * mm, "end": v(17.37, 30.86) * mm});
            skPoint(sketch, "E25.2.2", {"position": v(21.86, 27.86) * mm});
            skArc(sketch, "E25.2.3", {"start": v(18.32, 25.48) * mm, "mid": v(17.88, 25.23) * mm, "end": v(17.38, 25.34) * mm});
            skArc(sketch, "E25.2.4", {"start": v(17.37, 30.86) * mm, "mid": v(16.7, 31.23) * mm, "end": v(16, 31.59) * mm});
            skArc(sketch, "E25.2.5", {"start": v(16.76, 25.75) * mm, "mid": v(16.47, 26.17) * mm, "end": v(16.53, 26.68) * mm});
            skArc(sketch, "E25.2.6", {"start": v(17.38, 25.34) * mm, "mid": v(17.07, 25.55) * mm, "end": v(16.76, 25.75) * mm});
            skArc(sketch, "E25.3.0", {"start": v(22.94, 21.42) * mm, "mid": v(24.78, 22.54) * mm, "end": v(26.88, 23.06) * mm});
            skArc(sketch, "E25.3.1", {"start": v(21.42, 22.94) * mm, "mid": v(22.54, 24.78) * mm, "end": v(23.06, 26.88) * mm});
            skPoint(sketch, "E25.3.2", {"position": v(26.88, 23.06) * mm});
            skArc(sketch, "E25.3.3", {"start": v(22.94, 21.42) * mm, "mid": v(22.45, 21.25) * mm, "end": v(21.99, 21.46) * mm});
            skArc(sketch, "E25.3.4", {"start": v(23.06, 26.88) * mm, "mid": v(22.47, 27.37) * mm, "end": v(21.86, 27.86) * mm});
            skArc(sketch, "E25.3.5", {"start": v(21.46, 21.99) * mm, "mid": v(21.25, 22.45) * mm, "end": v(21.42, 22.94) * mm});
            skArc(sketch, "E25.3.6", {"start": v(21.99, 21.46) * mm, "mid": v(21.73, 21.73) * mm, "end": v(21.46, 21.99) * mm});
            skArc(sketch, "E25.4.0", {"start": v(26.68, 16.53) * mm, "mid": v(28.7, 17.28) * mm, "end": v(30.86, 17.37) * mm});
            skArc(sketch, "E25.4.1", {"start": v(25.48, 18.32) * mm, "mid": v(26.94, 19.9) * mm, "end": v(27.86, 21.86) * mm});
            skPoint(sketch, "E25.4.2", {"position": v(30.86, 17.37) * mm});
            skArc(sketch, "E25.4.3", {"start": v(26.68, 16.53) * mm, "mid": v(26.17, 16.47) * mm, "end": v(25.75, 16.76) * mm});
            skArc(sketch, "E25.4.4", {"start": v(27.86, 21.86) * mm, "mid": v(27.37, 22.47) * mm, "end": v(26.88, 23.06) * mm});
            skArc(sketch, "E25.4.5", {"start": v(25.34, 17.38) * mm, "mid": v(25.23, 17.88) * mm, "end": v(25.48, 18.32) * mm});
            skArc(sketch, "E25.4.6", {"start": v(25.75, 16.76) * mm, "mid": v(25.55, 17.07) * mm, "end": v(25.34, 17.38) * mm});
            skArc(sketch, "E25.5.0", {"start": v(29.39, 11) * mm, "mid": v(31.52, 11.34) * mm, "end": v(33.66, 11.02) * mm});
            skArc(sketch, "E25.5.1", {"start": v(28.57, 13) * mm, "mid": v(30.31, 14.27) * mm, "end": v(31.59, 16) * mm});
            skPoint(sketch, "E25.5.2", {"position": v(33.66, 11.02) * mm});
            skArc(sketch, "E25.5.3", {"start": v(29.39, 11) * mm, "mid": v(28.88, 11.04) * mm, "end": v(28.53, 11.42) * mm});
            skArc(sketch, "E25.5.4", {"start": v(31.59, 16) * mm, "mid": v(31.23, 16.7) * mm, "end": v(30.86, 17.37) * mm});
            skArc(sketch, "E25.5.5", {"start": v(28.24, 12.1) * mm, "mid": v(28.23, 12.61) * mm, "end": v(28.57, 13) * mm});
            skArc(sketch, "E25.5.6", {"start": v(28.53, 11.42) * mm, "mid": v(28.39, 11.76) * mm, "end": v(28.24, 12.1) * mm});
            skArc(sketch, "E25.6.0", {"start": v(30.97, 5.06) * mm, "mid": v(33.13, 4.98) * mm, "end": v(35.16, 4.24) * mm});
            skArc(sketch, "E25.6.1", {"start": v(30.55, 7.17) * mm, "mid": v(32.51, 8.08) * mm, "end": v(34.1, 9.54) * mm});
            skPoint(sketch, "E25.6.2", {"position": v(35.16, 4.24) * mm});
            skArc(sketch, "E25.6.3", {"start": v(30.97, 5.06) * mm, "mid": v(30.48, 5.2) * mm, "end": v(30.2, 5.63) * mm});
            skArc(sketch, "E25.6.4", {"start": v(34.1, 9.54) * mm, "mid": v(33.89, 10.28) * mm, "end": v(33.66, 11.02) * mm});
            skArc(sketch, "E25.6.5", {"start": v(30.06, 6.36) * mm, "mid": v(30.15, 6.86) * mm, "end": v(30.55, 7.17) * mm});
            skArc(sketch, "E25.6.6", {"start": v(30.2, 5.63) * mm, "mid": v(30.14, 6) * mm, "end": v(30.06, 6.36) * mm});
            skArc(sketch, "E25.7.0", {"start": v(31.37, -1.07) * mm, "mid": v(33.46, -1.58) * mm, "end": v(35.3, -2.7) * mm});
            skArc(sketch, "E25.7.1", {"start": v(31.37, 1.07) * mm, "mid": v(33.46, 1.58) * mm, "end": v(35.3, 2.7) * mm});
            skPoint(sketch, "E25.7.2", {"position": v(35.3, -2.7) * mm});
            skArc(sketch, "E25.7.3", {"start": v(31.37, -1.07) * mm, "mid": v(30.9, -0.85) * mm, "end": v(30.72, -0.37) * mm});
            skArc(sketch, "E25.7.4", {"start": v(35.3, 2.7) * mm, "mid": v(35.24, 3.47) * mm, "end": v(35.16, 4.24) * mm});
            skArc(sketch, "E25.7.5", {"start": v(30.72, 0.37) * mm, "mid": v(30.9, 0.85) * mm, "end": v(31.37, 1.07) * mm});
            skArc(sketch, "E25.7.6", {"start": v(30.72, -0.37) * mm, "mid": v(30.73, 0) * mm, "end": v(30.72, 0.37) * mm});
            skArc(sketch, "E25.8.0", {"start": v(30.55, -7.17) * mm, "mid": v(32.51, -8.08) * mm, "end": v(34.1, -9.54) * mm});
            skArc(sketch, "E25.8.1", {"start": v(30.97, -5.06) * mm, "mid": v(33.13, -4.98) * mm, "end": v(35.16, -4.24) * mm});
            skPoint(sketch, "E25.8.2", {"position": v(34.1, -9.54) * mm});
            skArc(sketch, "E25.8.3", {"start": v(30.55, -7.17) * mm, "mid": v(30.15, -6.86) * mm, "end": v(30.06, -6.36) * mm});
            skArc(sketch, "E25.8.4", {"start": v(35.16, -4.24) * mm, "mid": v(35.24, -3.47) * mm, "end": v(35.3, -2.7) * mm});
            skArc(sketch, "E25.8.5", {"start": v(30.2, -5.63) * mm, "mid": v(30.48, -5.2) * mm, "end": v(30.97, -5.06) * mm});
            skArc(sketch, "E25.8.6", {"start": v(30.06, -6.36) * mm, "mid": v(30.14, -6) * mm, "end": v(30.2, -5.63) * mm});
            skArc(sketch, "E25.9.0", {"start": v(28.57, -13) * mm, "mid": v(30.31, -14.27) * mm, "end": v(31.59, -16) * mm});
            skArc(sketch, "E25.9.1", {"start": v(29.39, -11) * mm, "mid": v(31.52, -11.34) * mm, "end": v(33.66, -11.02) * mm});
            skPoint(sketch, "E25.9.2", {"position": v(31.59, -16) * mm});
            skArc(sketch, "E25.9.3", {"start": v(28.57, -13) * mm, "mid": v(28.23, -12.61) * mm, "end": v(28.24, -12.1) * mm});
            skArc(sketch, "E25.9.4", {"start": v(33.66, -11.02) * mm, "mid": v(33.89, -10.28) * mm, "end": v(34.1, -9.54) * mm});
            skArc(sketch, "E25.9.5", {"start": v(28.53, -11.42) * mm, "mid": v(28.88, -11.04) * mm, "end": v(29.39, -11) * mm});
            skArc(sketch, "E25.9.6", {"start": v(28.24, -12.1) * mm, "mid": v(28.39, -11.76) * mm, "end": v(28.53, -11.42) * mm});
            skArc(sketch, "E25.10.0", {"start": v(25.48, -18.32) * mm, "mid": v(26.94, -19.9) * mm, "end": v(27.86, -21.86) * mm});
            skArc(sketch, "E25.10.1", {"start": v(26.68, -16.53) * mm, "mid": v(28.7, -17.28) * mm, "end": v(30.86, -17.37) * mm});
            skPoint(sketch, "E25.10.2", {"position": v(27.86, -21.86) * mm});
            skArc(sketch, "E25.10.3", {"start": v(25.48, -18.32) * mm, "mid": v(25.23, -17.88) * mm, "end": v(25.34, -17.38) * mm});
            skArc(sketch, "E25.10.4", {"start": v(30.86, -17.37) * mm, "mid": v(31.23, -16.7) * mm, "end": v(31.59, -16) * mm});
            skArc(sketch, "E25.10.5", {"start": v(25.75, -16.76) * mm, "mid": v(26.17, -16.47) * mm, "end": v(26.68, -16.53) * mm});
            skArc(sketch, "E25.10.6", {"start": v(25.34, -17.38) * mm, "mid": v(25.55, -17.07) * mm, "end": v(25.75, -16.76) * mm});
            skArc(sketch, "E25.11.0", {"start": v(21.42, -22.94) * mm, "mid": v(22.54, -24.78) * mm, "end": v(23.06, -26.88) * mm});
            skArc(sketch, "E25.11.1", {"start": v(22.94, -21.42) * mm, "mid": v(24.78, -22.54) * mm, "end": v(26.88, -23.06) * mm});
            skPoint(sketch, "E25.11.2", {"position": v(23.06, -26.88) * mm});
            skArc(sketch, "E25.11.3", {"start": v(21.42, -22.94) * mm, "mid": v(21.25, -22.45) * mm, "end": v(21.46, -21.99) * mm});
            skArc(sketch, "E25.11.4", {"start": v(26.88, -23.06) * mm, "mid": v(27.37, -22.47) * mm, "end": v(27.86, -21.86) * mm});
            skArc(sketch, "E25.11.5", {"start": v(21.99, -21.46) * mm, "mid": v(22.45, -21.25) * mm, "end": v(22.94, -21.42) * mm});
            skArc(sketch, "E25.11.6", {"start": v(21.46, -21.99) * mm, "mid": v(21.73, -21.73) * mm, "end": v(21.99, -21.46) * mm});
            skArc(sketch, "E25.12.0", {"start": v(16.53, -26.68) * mm, "mid": v(17.28, -28.7) * mm, "end": v(17.37, -30.86) * mm});
            skArc(sketch, "E25.12.1", {"start": v(18.32, -25.48) * mm, "mid": v(19.9, -26.94) * mm, "end": v(21.86, -27.86) * mm});
            skPoint(sketch, "E25.12.2", {"position": v(17.37, -30.86) * mm});
            skArc(sketch, "E25.12.3", {"start": v(16.53, -26.68) * mm, "mid": v(16.47, -26.17) * mm, "end": v(16.76, -25.75) * mm});
            skArc(sketch, "E25.12.4", {"start": v(21.86, -27.86) * mm, "mid": v(22.47, -27.37) * mm, "end": v(23.06, -26.88) * mm});
            skArc(sketch, "E25.12.5", {"start": v(17.38, -25.34) * mm, "mid": v(17.88, -25.23) * mm, "end": v(18.32, -25.48) * mm});
            skArc(sketch, "E25.12.6", {"start": v(16.76, -25.75) * mm, "mid": v(17.07, -25.55) * mm, "end": v(17.38, -25.34) * mm});
            skArc(sketch, "E25.13.0", {"start": v(11, -29.39) * mm, "mid": v(11.34, -31.52) * mm, "end": v(11.02, -33.66) * mm});
            skArc(sketch, "E25.13.1", {"start": v(13, -28.57) * mm, "mid": v(14.27, -30.31) * mm, "end": v(16, -31.59) * mm});
            skPoint(sketch, "E25.13.2", {"position": v(11.02, -33.66) * mm});
            skArc(sketch, "E25.13.3", {"start": v(11, -29.39) * mm, "mid": v(11.04, -28.88) * mm, "end": v(11.42, -28.53) * mm});
            skArc(sketch, "E25.13.4", {"start": v(16, -31.59) * mm, "mid": v(16.7, -31.23) * mm, "end": v(17.37, -30.86) * mm});
            skArc(sketch, "E25.13.5", {"start": v(12.1, -28.24) * mm, "mid": v(12.61, -28.23) * mm, "end": v(13, -28.57) * mm});
            skArc(sketch, "E25.13.6", {"start": v(11.42, -28.53) * mm, "mid": v(11.76, -28.39) * mm, "end": v(12.1, -28.24) * mm});
            skArc(sketch, "E25.14.0", {"start": v(5.06, -30.97) * mm, "mid": v(4.98, -33.13) * mm, "end": v(4.24, -35.16) * mm});
            skArc(sketch, "E25.14.1", {"start": v(7.17, -30.55) * mm, "mid": v(8.08, -32.51) * mm, "end": v(9.54, -34.1) * mm});
            skPoint(sketch, "E25.14.2", {"position": v(4.24, -35.16) * mm});
            skArc(sketch, "E25.14.3", {"start": v(5.06, -30.97) * mm, "mid": v(5.2, -30.48) * mm, "end": v(5.63, -30.2) * mm});
            skArc(sketch, "E25.14.4", {"start": v(9.54, -34.1) * mm, "mid": v(10.28, -33.89) * mm, "end": v(11.02, -33.66) * mm});
            skArc(sketch, "E25.14.5", {"start": v(6.36, -30.06) * mm, "mid": v(6.86, -30.15) * mm, "end": v(7.17, -30.55) * mm});
            skArc(sketch, "E25.14.6", {"start": v(5.63, -30.2) * mm, "mid": v(6, -30.14) * mm, "end": v(6.36, -30.06) * mm});
            skArc(sketch, "E25.15.0", {"start": v(-1.07, -31.37) * mm, "mid": v(-1.58, -33.46) * mm, "end": v(-2.7, -35.3) * mm});
            skArc(sketch, "E25.15.1", {"start": v(1.07, -31.37) * mm, "mid": v(1.58, -33.46) * mm, "end": v(2.7, -35.3) * mm});
            skPoint(sketch, "E25.15.2", {"position": v(-2.7, -35.3) * mm});
            skArc(sketch, "E25.15.3", {"start": v(-1.07, -31.37) * mm, "mid": v(-0.85, -30.9) * mm, "end": v(-0.37, -30.72) * mm});
            skArc(sketch, "E25.15.4", {"start": v(2.7, -35.3) * mm, "mid": v(3.47, -35.24) * mm, "end": v(4.24, -35.16) * mm});
            skArc(sketch, "E25.15.5", {"start": v(0.37, -30.72) * mm, "mid": v(0.85, -30.9) * mm, "end": v(1.07, -31.37) * mm});
            skArc(sketch, "E25.15.6", {"start": v(-0.37, -30.72) * mm, "mid": v(0, -30.73) * mm, "end": v(0.37, -30.72) * mm});
            skArc(sketch, "E25.16.0", {"start": v(-7.17, -30.55) * mm, "mid": v(-8.08, -32.51) * mm, "end": v(-9.54, -34.1) * mm});
            skArc(sketch, "E25.16.1", {"start": v(-5.06, -30.97) * mm, "mid": v(-4.98, -33.13) * mm, "end": v(-4.24, -35.16) * mm});
            skPoint(sketch, "E25.16.2", {"position": v(-9.54, -34.1) * mm});
            skArc(sketch, "E25.16.3", {"start": v(-7.17, -30.55) * mm, "mid": v(-6.86, -30.15) * mm, "end": v(-6.36, -30.06) * mm});
            skArc(sketch, "E25.16.4", {"start": v(-4.24, -35.16) * mm, "mid": v(-3.47, -35.24) * mm, "end": v(-2.7, -35.3) * mm});
            skArc(sketch, "E25.16.5", {"start": v(-5.63, -30.2) * mm, "mid": v(-5.2, -30.48) * mm, "end": v(-5.06, -30.97) * mm});
            skArc(sketch, "E25.16.6", {"start": v(-6.36, -30.06) * mm, "mid": v(-6, -30.14) * mm, "end": v(-5.63, -30.2) * mm});
            skArc(sketch, "E25.17.0", {"start": v(-13, -28.57) * mm, "mid": v(-14.27, -30.31) * mm, "end": v(-16, -31.59) * mm});
            skArc(sketch, "E25.17.1", {"start": v(-11, -29.39) * mm, "mid": v(-11.34, -31.52) * mm, "end": v(-11.02, -33.66) * mm});
            skPoint(sketch, "E25.17.2", {"position": v(-16, -31.59) * mm});
            skArc(sketch, "E25.17.3", {"start": v(-13, -28.57) * mm, "mid": v(-12.61, -28.23) * mm, "end": v(-12.1, -28.24) * mm});
            skArc(sketch, "E25.17.4", {"start": v(-11.02, -33.66) * mm, "mid": v(-10.28, -33.89) * mm, "end": v(-9.54, -34.1) * mm});
            skArc(sketch, "E25.17.5", {"start": v(-11.42, -28.53) * mm, "mid": v(-11.04, -28.88) * mm, "end": v(-11, -29.39) * mm});
            skArc(sketch, "E25.17.6", {"start": v(-12.1, -28.24) * mm, "mid": v(-11.76, -28.39) * mm, "end": v(-11.42, -28.53) * mm});
            skArc(sketch, "E25.18.0", {"start": v(-18.32, -25.48) * mm, "mid": v(-19.9, -26.94) * mm, "end": v(-21.86, -27.86) * mm});
            skArc(sketch, "E25.18.1", {"start": v(-16.53, -26.68) * mm, "mid": v(-17.28, -28.7) * mm, "end": v(-17.37, -30.86) * mm});
            skPoint(sketch, "E25.18.2", {"position": v(-21.86, -27.86) * mm});
            skArc(sketch, "E25.18.3", {"start": v(-18.32, -25.48) * mm, "mid": v(-17.88, -25.23) * mm, "end": v(-17.38, -25.34) * mm});
            skArc(sketch, "E25.18.4", {"start": v(-17.37, -30.86) * mm, "mid": v(-16.7, -31.23) * mm, "end": v(-16, -31.59) * mm});
            skArc(sketch, "E25.18.5", {"start": v(-16.76, -25.75) * mm, "mid": v(-16.47, -26.17) * mm, "end": v(-16.53, -26.68) * mm});
            skArc(sketch, "E25.18.6", {"start": v(-17.38, -25.34) * mm, "mid": v(-17.07, -25.55) * mm, "end": v(-16.76, -25.75) * mm});
            skArc(sketch, "E25.19.0", {"start": v(-22.94, -21.42) * mm, "mid": v(-24.78, -22.54) * mm, "end": v(-26.88, -23.06) * mm});
            skArc(sketch, "E25.19.1", {"start": v(-21.42, -22.94) * mm, "mid": v(-22.54, -24.78) * mm, "end": v(-23.06, -26.88) * mm});
            skPoint(sketch, "E25.19.2", {"position": v(-26.88, -23.06) * mm});
            skArc(sketch, "E25.19.3", {"start": v(-22.94, -21.42) * mm, "mid": v(-22.45, -21.25) * mm, "end": v(-21.99, -21.46) * mm});
            skArc(sketch, "E25.19.4", {"start": v(-23.06, -26.88) * mm, "mid": v(-22.47, -27.37) * mm, "end": v(-21.86, -27.86) * mm});
            skArc(sketch, "E25.19.5", {"start": v(-21.46, -21.99) * mm, "mid": v(-21.25, -22.45) * mm, "end": v(-21.42, -22.94) * mm});
            skArc(sketch, "E25.19.6", {"start": v(-21.99, -21.46) * mm, "mid": v(-21.73, -21.73) * mm, "end": v(-21.46, -21.99) * mm});
            skArc(sketch, "E25.20.0", {"start": v(-26.68, -16.53) * mm, "mid": v(-28.7, -17.28) * mm, "end": v(-30.86, -17.37) * mm});
            skArc(sketch, "E25.20.1", {"start": v(-25.48, -18.32) * mm, "mid": v(-26.94, -19.9) * mm, "end": v(-27.86, -21.86) * mm});
            skPoint(sketch, "E25.20.2", {"position": v(-30.86, -17.37) * mm});
            skArc(sketch, "E25.20.3", {"start": v(-26.68, -16.53) * mm, "mid": v(-26.17, -16.47) * mm, "end": v(-25.75, -16.76) * mm});
            skArc(sketch, "E25.20.4", {"start": v(-27.86, -21.86) * mm, "mid": v(-27.37, -22.47) * mm, "end": v(-26.88, -23.06) * mm});
            skArc(sketch, "E25.20.5", {"start": v(-25.34, -17.38) * mm, "mid": v(-25.23, -17.88) * mm, "end": v(-25.48, -18.32) * mm});
            skArc(sketch, "E25.20.6", {"start": v(-25.75, -16.76) * mm, "mid": v(-25.55, -17.07) * mm, "end": v(-25.34, -17.38) * mm});
            skArc(sketch, "E25.21.0", {"start": v(-29.39, -11) * mm, "mid": v(-31.52, -11.34) * mm, "end": v(-33.66, -11.02) * mm});
            skArc(sketch, "E25.21.1", {"start": v(-28.57, -13) * mm, "mid": v(-30.31, -14.27) * mm, "end": v(-31.59, -16) * mm});
            skPoint(sketch, "E25.21.2", {"position": v(-33.66, -11.02) * mm});
            skArc(sketch, "E25.21.3", {"start": v(-29.39, -11) * mm, "mid": v(-28.88, -11.04) * mm, "end": v(-28.53, -11.42) * mm});
            skArc(sketch, "E25.21.4", {"start": v(-31.59, -16) * mm, "mid": v(-31.23, -16.7) * mm, "end": v(-30.86, -17.37) * mm});
            skArc(sketch, "E25.21.5", {"start": v(-28.24, -12.1) * mm, "mid": v(-28.23, -12.61) * mm, "end": v(-28.57, -13) * mm});
            skArc(sketch, "E25.21.6", {"start": v(-28.53, -11.42) * mm, "mid": v(-28.39, -11.76) * mm, "end": v(-28.24, -12.1) * mm});
            skArc(sketch, "E25.22.0", {"start": v(-30.97, -5.06) * mm, "mid": v(-33.13, -4.98) * mm, "end": v(-35.16, -4.24) * mm});
            skArc(sketch, "E25.22.1", {"start": v(-30.55, -7.17) * mm, "mid": v(-32.51, -8.08) * mm, "end": v(-34.1, -9.54) * mm});
            skPoint(sketch, "E25.22.2", {"position": v(-35.16, -4.24) * mm});
            skArc(sketch, "E25.22.3", {"start": v(-30.97, -5.06) * mm, "mid": v(-30.48, -5.2) * mm, "end": v(-30.2, -5.63) * mm});
            skArc(sketch, "E25.22.4", {"start": v(-34.1, -9.54) * mm, "mid": v(-33.89, -10.28) * mm, "end": v(-33.66, -11.02) * mm});
            skArc(sketch, "E25.22.5", {"start": v(-30.06, -6.36) * mm, "mid": v(-30.15, -6.86) * mm, "end": v(-30.55, -7.17) * mm});
            skArc(sketch, "E25.22.6", {"start": v(-30.2, -5.63) * mm, "mid": v(-30.14, -6) * mm, "end": v(-30.06, -6.36) * mm});
            skArc(sketch, "E25.23.0", {"start": v(-31.37, 1.07) * mm, "mid": v(-33.46, 1.58) * mm, "end": v(-35.3, 2.7) * mm});
            skArc(sketch, "E25.23.1", {"start": v(-31.37, -1.07) * mm, "mid": v(-33.46, -1.58) * mm, "end": v(-35.3, -2.7) * mm});
            skPoint(sketch, "E25.23.2", {"position": v(-35.3, 2.7) * mm});
            skArc(sketch, "E25.23.3", {"start": v(-31.37, 1.07) * mm, "mid": v(-30.9, 0.85) * mm, "end": v(-30.72, 0.37) * mm});
            skArc(sketch, "E25.23.4", {"start": v(-35.3, -2.7) * mm, "mid": v(-35.24, -3.47) * mm, "end": v(-35.16, -4.24) * mm});
            skArc(sketch, "E25.23.5", {"start": v(-30.72, -0.37) * mm, "mid": v(-30.9, -0.85) * mm, "end": v(-31.37, -1.07) * mm});
            skArc(sketch, "E25.23.6", {"start": v(-30.72, 0.37) * mm, "mid": v(-30.73, 0) * mm, "end": v(-30.72, -0.37) * mm});
            skArc(sketch, "E25.24.0", {"start": v(-30.55, 7.17) * mm, "mid": v(-32.51, 8.08) * mm, "end": v(-34.1, 9.54) * mm});
            skArc(sketch, "E25.24.1", {"start": v(-30.97, 5.06) * mm, "mid": v(-33.13, 4.98) * mm, "end": v(-35.16, 4.24) * mm});
            skPoint(sketch, "E25.24.2", {"position": v(-34.1, 9.54) * mm});
            skArc(sketch, "E25.24.3", {"start": v(-30.55, 7.17) * mm, "mid": v(-30.15, 6.86) * mm, "end": v(-30.06, 6.36) * mm});
            skArc(sketch, "E25.24.4", {"start": v(-35.16, 4.24) * mm, "mid": v(-35.24, 3.47) * mm, "end": v(-35.3, 2.7) * mm});
            skArc(sketch, "E25.24.5", {"start": v(-30.2, 5.63) * mm, "mid": v(-30.48, 5.2) * mm, "end": v(-30.97, 5.06) * mm});
            skArc(sketch, "E25.24.6", {"start": v(-30.06, 6.36) * mm, "mid": v(-30.14, 6) * mm, "end": v(-30.2, 5.63) * mm});
            skArc(sketch, "E25.25.0", {"start": v(-28.57, 13) * mm, "mid": v(-30.31, 14.27) * mm, "end": v(-31.59, 16) * mm});
            skArc(sketch, "E25.25.1", {"start": v(-29.39, 11) * mm, "mid": v(-31.52, 11.34) * mm, "end": v(-33.66, 11.02) * mm});
            skPoint(sketch, "E25.25.2", {"position": v(-31.59, 16) * mm});
            skArc(sketch, "E25.25.3", {"start": v(-28.57, 13) * mm, "mid": v(-28.23, 12.61) * mm, "end": v(-28.24, 12.1) * mm});
            skArc(sketch, "E25.25.4", {"start": v(-33.66, 11.02) * mm, "mid": v(-33.89, 10.28) * mm, "end": v(-34.1, 9.54) * mm});
            skArc(sketch, "E25.25.5", {"start": v(-28.53, 11.42) * mm, "mid": v(-28.88, 11.04) * mm, "end": v(-29.39, 11) * mm});
            skArc(sketch, "E25.25.6", {"start": v(-28.24, 12.1) * mm, "mid": v(-28.39, 11.76) * mm, "end": v(-28.53, 11.42) * mm});
            skArc(sketch, "E25.26.0", {"start": v(-25.48, 18.32) * mm, "mid": v(-26.94, 19.9) * mm, "end": v(-27.86, 21.86) * mm});
            skArc(sketch, "E25.26.1", {"start": v(-26.68, 16.53) * mm, "mid": v(-28.7, 17.28) * mm, "end": v(-30.86, 17.37) * mm});
            skPoint(sketch, "E25.26.2", {"position": v(-27.86, 21.86) * mm});
            skArc(sketch, "E25.26.3", {"start": v(-25.48, 18.32) * mm, "mid": v(-25.23, 17.88) * mm, "end": v(-25.34, 17.38) * mm});
            skArc(sketch, "E25.26.4", {"start": v(-30.86, 17.37) * mm, "mid": v(-31.23, 16.7) * mm, "end": v(-31.59, 16) * mm});
            skArc(sketch, "E25.26.5", {"start": v(-25.75, 16.76) * mm, "mid": v(-26.17, 16.47) * mm, "end": v(-26.68, 16.53) * mm});
            skArc(sketch, "E25.26.6", {"start": v(-25.34, 17.38) * mm, "mid": v(-25.55, 17.07) * mm, "end": v(-25.75, 16.76) * mm});
            skArc(sketch, "E25.27.0", {"start": v(-21.42, 22.94) * mm, "mid": v(-22.54, 24.78) * mm, "end": v(-23.06, 26.88) * mm});
            skArc(sketch, "E25.27.1", {"start": v(-22.94, 21.42) * mm, "mid": v(-24.78, 22.54) * mm, "end": v(-26.88, 23.06) * mm});
            skPoint(sketch, "E25.27.2", {"position": v(-23.06, 26.88) * mm});
            skArc(sketch, "E25.27.3", {"start": v(-21.42, 22.94) * mm, "mid": v(-21.25, 22.45) * mm, "end": v(-21.46, 21.99) * mm});
            skArc(sketch, "E25.27.4", {"start": v(-26.88, 23.06) * mm, "mid": v(-27.37, 22.47) * mm, "end": v(-27.86, 21.86) * mm});
            skArc(sketch, "E25.27.5", {"start": v(-21.99, 21.46) * mm, "mid": v(-22.45, 21.25) * mm, "end": v(-22.94, 21.42) * mm});
            skArc(sketch, "E25.27.6", {"start": v(-21.46, 21.99) * mm, "mid": v(-21.73, 21.73) * mm, "end": v(-21.99, 21.46) * mm});
            skArc(sketch, "E25.28.0", {"start": v(-16.53, 26.68) * mm, "mid": v(-17.28, 28.7) * mm, "end": v(-17.37, 30.86) * mm});
            skArc(sketch, "E25.28.1", {"start": v(-18.32, 25.48) * mm, "mid": v(-19.9, 26.94) * mm, "end": v(-21.86, 27.86) * mm});
            skPoint(sketch, "E25.28.2", {"position": v(-17.37, 30.86) * mm});
            skArc(sketch, "E25.28.3", {"start": v(-16.53, 26.68) * mm, "mid": v(-16.47, 26.17) * mm, "end": v(-16.76, 25.75) * mm});
            skArc(sketch, "E25.28.4", {"start": v(-21.86, 27.86) * mm, "mid": v(-22.47, 27.37) * mm, "end": v(-23.06, 26.88) * mm});
            skArc(sketch, "E25.28.5", {"start": v(-17.38, 25.34) * mm, "mid": v(-17.88, 25.23) * mm, "end": v(-18.32, 25.48) * mm});
            skArc(sketch, "E25.28.6", {"start": v(-16.76, 25.75) * mm, "mid": v(-17.07, 25.55) * mm, "end": v(-17.38, 25.34) * mm});
            skArc(sketch, "E25.29.0", {"start": v(-11, 29.39) * mm, "mid": v(-11.34, 31.52) * mm, "end": v(-11.02, 33.66) * mm});
            skArc(sketch, "E25.29.1", {"start": v(-13, 28.57) * mm, "mid": v(-14.27, 30.31) * mm, "end": v(-16, 31.59) * mm});
            skPoint(sketch, "E25.29.2", {"position": v(-11.02, 33.66) * mm});
            skArc(sketch, "E25.29.3", {"start": v(-11, 29.39) * mm, "mid": v(-11.04, 28.88) * mm, "end": v(-11.42, 28.53) * mm});
            skArc(sketch, "E25.29.4", {"start": v(-16, 31.59) * mm, "mid": v(-16.7, 31.23) * mm, "end": v(-17.37, 30.86) * mm});
            skArc(sketch, "E25.29.5", {"start": v(-12.1, 28.24) * mm, "mid": v(-12.61, 28.23) * mm, "end": v(-13, 28.57) * mm});
            skArc(sketch, "E25.29.6", {"start": v(-11.42, 28.53) * mm, "mid": v(-11.76, 28.39) * mm, "end": v(-12.1, 28.24) * mm});
            skArc(sketch, "E25.30.0", {"start": v(-5.06, 30.97) * mm, "mid": v(-4.98, 33.13) * mm, "end": v(-4.24, 35.16) * mm});
            skArc(sketch, "E25.30.1", {"start": v(-7.17, 30.55) * mm, "mid": v(-8.08, 32.51) * mm, "end": v(-9.54, 34.1) * mm});
            skPoint(sketch, "E25.30.2", {"position": v(-4.24, 35.16) * mm});
            skArc(sketch, "E25.30.3", {"start": v(-5.06, 30.97) * mm, "mid": v(-5.2, 30.48) * mm, "end": v(-5.63, 30.2) * mm});
            skArc(sketch, "E25.30.4", {"start": v(-9.54, 34.1) * mm, "mid": v(-10.28, 33.89) * mm, "end": v(-11.02, 33.66) * mm});
            skArc(sketch, "E25.30.5", {"start": v(-6.36, 30.06) * mm, "mid": v(-6.86, 30.15) * mm, "end": v(-7.17, 30.55) * mm});
            skArc(sketch, "E25.30.6", {"start": v(-5.63, 30.2) * mm, "mid": v(-6, 30.14) * mm, "end": v(-6.36, 30.06) * mm});
            skArc(sketch, "E25.31.0", {"start": v(1.07, 31.37) * mm, "mid": v(1.58, 33.46) * mm, "end": v(2.7, 35.3) * mm});
            skArc(sketch, "E25.31.1", {"start": v(-1.07, 31.37) * mm, "mid": v(-1.58, 33.46) * mm, "end": v(-2.7, 35.3) * mm});
            skPoint(sketch, "E25.31.2", {"position": v(2.7, 35.3) * mm});
            skArc(sketch, "E25.31.3", {"start": v(1.07, 31.37) * mm, "mid": v(0.85, 30.9) * mm, "end": v(0.37, 30.72) * mm});
            skArc(sketch, "E25.31.4", {"start": v(-2.7, 35.3) * mm, "mid": v(-3.47, 35.24) * mm, "end": v(-4.24, 35.16) * mm});
            skArc(sketch, "E25.31.5", {"start": v(-0.37, 30.72) * mm, "mid": v(-0.85, 30.9) * mm, "end": v(-1.07, 31.37) * mm});
            skArc(sketch, "E25.31.6", {"start": v(0.37, 30.72) * mm, "mid": v(0, 30.73) * mm, "end": v(-0.37, 30.72) * mm});
            skLineSegment(sketch, "E25.anchor1", {"start": v(0, 0) * mm, "end": v(-1.94, 31.76) * mm, "construction": true});
            skLineSegment(sketch, "E25.anchor2", {"start": v(0, 0) * mm, "end": v(-8.1, 30.77) * mm, "construction": true});
            skSolve(sketch);
        }
        {
            var Q0;
            Q0=makeQuery(id+"F4.imprint","IMPRINT",FACE,{"disambiguationData":[TD([[makeQuery(id+"F4.imprint","IMPRINT",EDGE,{"derivedFrom":sQuery(id+"F4.wireOp",EDGE,"E18.0")}),1.0]])]});
            extrude(context, id + "F5", {"entities" : qUnion([Q0]), "depth" : 3 * mm, "offsetDistance" : 25 * mm});
        }
        {
            var Q0;
            Q0=makeQuery(id+"F5.opExtrude","CAP_FACE",FACE,{"disambiguationData":[OSD([sQuery(id+"F4.wireOp",EDGE,"E18.0"),sQuery(id+"F4.wireOp",EDGE,"E19.0"),sQuery(id+"F4.wireOp",EDGE,"E20.0"),sQuery(id+"F4.wireOp",EDGE,"E21.0"),sQuery(id+"F4.wireOp",EDGE,"E23"),sQuery(id+"F4.wireOp",EDGE,"E24"),sQuery(id+"F4.wireOp",EDGE,"E25.1.0"),sQuery(id+"F4.wireOp",EDGE,"E25.1.1"),sQuery(id+"F4.wireOp",EDGE,"E25.1.3"),sQuery(id+"F4.wireOp",EDGE,"E25.1.4"),sQuery(id+"F4.wireOp",EDGE,"E25.1.5"),sQuery(id+"F4.wireOp",EDGE,"E25.1.6"),sQuery(id+"F4.wireOp",EDGE,"E25.2.0"),sQuery(id+"F4.wireOp",EDGE,"E25.2.1"),sQuery(id+"F4.wireOp",EDGE,"E25.2.3"),sQuery(id+"F4.wireOp",EDGE,"E25.2.4"),sQuery(id+"F4.wireOp",EDGE,"E25.2.5"),sQuery(id+"F4.wireOp",EDGE,"E25.2.6"),sQuery(id+"F4.wireOp",EDGE,"E25.3.0"),sQuery(id+"F4.wireOp",EDGE,"E25.3.1"),sQuery(id+"F4.wireOp",EDGE,"E25.3.3"),sQuery(id+"F4.wireOp",EDGE,"E25.3.4"),sQuery(id+"F4.wireOp",EDGE,"E25.3.5"),sQuery(id+"F4.wireOp",EDGE,"E25.3.6"),sQuery(id+"F4.wireOp",EDGE,"E25.4.0"),sQuery(id+"F4.wireOp",EDGE,"E25.4.1"),sQuery(id+"F4.wireOp",EDGE,"E25.4.3"),sQuery(id+"F4.wireOp",EDGE,"E25.4.4"),sQuery(id+"F4.wireOp",EDGE,"E25.4.5"),sQuery(id+"F4.wireOp",EDGE,"E25.4.6"),sQuery(id+"F4.wireOp",EDGE,"E25.5.0"),sQuery(id+"F4.wireOp",EDGE,"E25.5.1"),sQuery(id+"F4.wireOp",EDGE,"E25.5.3"),sQuery(id+"F4.wireOp",EDGE,"E25.5.4"),sQuery(id+"F4.wireOp",EDGE,"E25.5.5"),sQuery(id+"F4.wireOp",EDGE,"E25.5.6"),sQuery(id+"F4.wireOp",EDGE,"E25.6.0"),sQuery(id+"F4.wireOp",EDGE,"E25.6.1"),sQuery(id+"F4.wireOp",EDGE,"E25.6.3"),sQuery(id+"F4.wireOp",EDGE,"E25.6.4"),sQuery(id+"F4.wireOp",EDGE,"E25.6.5"),sQuery(id+"F4.wireOp",EDGE,"E25.6.6"),sQuery(id+"F4.wireOp",EDGE,"E25.7.0"),sQuery(id+"F4.wireOp",EDGE,"E25.7.1"),sQuery(id+"F4.wireOp",EDGE,"E25.7.3"),sQuery(id+"F4.wireOp",EDGE,"E25.7.4"),sQuery(id+"F4.wireOp",EDGE,"E25.7.5"),sQuery(id+"F4.wireOp",EDGE,"E25.7.6"),sQuery(id+"F4.wireOp",EDGE,"E25.8.0"),sQuery(id+"F4.wireOp",EDGE,"E25.8.1"),sQuery(id+"F4.wireOp",EDGE,"E25.8.3"),sQuery(id+"F4.wireOp",EDGE,"E25.8.4"),sQuery(id+"F4.wireOp",EDGE,"E25.8.5"),sQuery(id+"F4.wireOp",EDGE,"E25.8.6"),sQuery(id+"F4.wireOp",EDGE,"E25.9.0"),sQuery(id+"F4.wireOp",EDGE,"E25.9.1"),sQuery(id+"F4.wireOp",EDGE,"E25.9.3"),sQuery(id+"F4.wireOp",EDGE,"E25.9.4"),sQuery(id+"F4.wireOp",EDGE,"E25.9.5"),sQuery(id+"F4.wireOp",EDGE,"E25.9.6"),sQuery(id+"F4.wireOp",EDGE,"E25.10.0"),sQuery(id+"F4.wireOp",EDGE,"E25.10.1"),sQuery(id+"F4.wireOp",EDGE,"E25.10.3"),sQuery(id+"F4.wireOp",EDGE,"E25.10.4"),sQuery(id+"F4.wireOp",EDGE,"E25.10.5"),sQuery(id+"F4.wireOp",EDGE,"E25.10.6"),sQuery(id+"F4.wireOp",EDGE,"E25.11.0"),sQuery(id+"F4.wireOp",EDGE,"E25.11.1"),sQuery(id+"F4.wireOp",EDGE,"E25.11.3"),sQuery(id+"F4.wireOp",EDGE,"E25.11.4"),sQuery(id+"F4.wireOp",EDGE,"E25.11.5"),sQuery(id+"F4.wireOp",EDGE,"E25.11.6"),sQuery(id+"F4.wireOp",EDGE,"E25.12.0"),sQuery(id+"F4.wireOp",EDGE,"E25.12.1"),sQuery(id+"F4.wireOp",EDGE,"E25.12.3"),sQuery(id+"F4.wireOp",EDGE,"E25.12.4"),sQuery(id+"F4.wireOp",EDGE,"E25.12.5"),sQuery(id+"F4.wireOp",EDGE,"E25.12.6"),sQuery(id+"F4.wireOp",EDGE,"E25.13.0"),sQuery(id+"F4.wireOp",EDGE,"E25.13.1"),sQuery(id+"F4.wireOp",EDGE,"E25.13.3"),sQuery(id+"F4.wireOp",EDGE,"E25.13.4"),sQuery(id+"F4.wireOp",EDGE,"E25.13.5"),sQuery(id+"F4.wireOp",EDGE,"E25.13.6"),sQuery(id+"F4.wireOp",EDGE,"E25.14.0"),sQuery(id+"F4.wireOp",EDGE,"E25.14.1"),sQuery(id+"F4.wireOp",EDGE,"E25.14.3"),sQuery(id+"F4.wireOp",EDGE,"E25.14.4"),sQuery(id+"F4.wireOp",EDGE,"E25.14.5"),sQuery(id+"F4.wireOp",EDGE,"E25.14.6"),sQuery(id+"F4.wireOp",EDGE,"E25.15.0"),sQuery(id+"F4.wireOp",EDGE,"E25.15.1"),sQuery(id+"F4.wireOp",EDGE,"E25.15.3"),sQuery(id+"F4.wireOp",EDGE,"E25.15.4"),sQuery(id+"F4.wireOp",EDGE,"E25.15.5"),sQuery(id+"F4.wireOp",EDGE,"E25.15.6"),sQuery(id+"F4.wireOp",EDGE,"E25.16.0"),sQuery(id+"F4.wireOp",EDGE,"E25.16.1"),sQuery(id+"F4.wireOp",EDGE,"E25.16.3"),sQuery(id+"F4.wireOp",EDGE,"E25.16.4"),sQuery(id+"F4.wireOp",EDGE,"E25.16.5"),sQuery(id+"F4.wireOp",EDGE,"E25.16.6"),sQuery(id+"F4.wireOp",EDGE,"E25.17.0"),sQuery(id+"F4.wireOp",EDGE,"E25.17.1"),sQuery(id+"F4.wireOp",EDGE,"E25.17.3"),sQuery(id+"F4.wireOp",EDGE,"E25.17.4"),sQuery(id+"F4.wireOp",EDGE,"E25.17.5"),sQuery(id+"F4.wireOp",EDGE,"E25.17.6"),sQuery(id+"F4.wireOp",EDGE,"E25.18.0"),sQuery(id+"F4.wireOp",EDGE,"E25.18.1"),sQuery(id+"F4.wireOp",EDGE,"E25.18.3"),sQuery(id+"F4.wireOp",EDGE,"E25.18.4"),sQuery(id+"F4.wireOp",EDGE,"E25.18.5"),sQuery(id+"F4.wireOp",EDGE,"E25.18.6"),sQuery(id+"F4.wireOp",EDGE,"E25.19.0"),sQuery(id+"F4.wireOp",EDGE,"E25.19.1"),sQuery(id+"F4.wireOp",EDGE,"E25.19.3"),sQuery(id+"F4.wireOp",EDGE,"E25.19.4"),sQuery(id+"F4.wireOp",EDGE,"E25.19.5"),sQuery(id+"F4.wireOp",EDGE,"E25.19.6"),sQuery(id+"F4.wireOp",EDGE,"E25.20.0"),sQuery(id+"F4.wireOp",EDGE,"E25.20.1"),sQuery(id+"F4.wireOp",EDGE,"E25.20.3"),sQuery(id+"F4.wireOp",EDGE,"E25.20.4"),sQuery(id+"F4.wireOp",EDGE,"E25.20.5"),sQuery(id+"F4.wireOp",EDGE,"E25.20.6"),sQuery(id+"F4.wireOp",EDGE,"E25.21.0"),sQuery(id+"F4.wireOp",EDGE,"E25.21.1"),sQuery(id+"F4.wireOp",EDGE,"E25.21.3"),sQuery(id+"F4.wireOp",EDGE,"E25.21.4"),sQuery(id+"F4.wireOp",EDGE,"E25.21.5"),sQuery(id+"F4.wireOp",EDGE,"E25.21.6"),sQuery(id+"F4.wireOp",EDGE,"E25.22.0"),sQuery(id+"F4.wireOp",EDGE,"E25.22.1"),sQuery(id+"F4.wireOp",EDGE,"E25.22.3"),sQuery(id+"F4.wireOp",EDGE,"E25.22.4"),sQuery(id+"F4.wireOp",EDGE,"E25.22.5"),sQuery(id+"F4.wireOp",EDGE,"E25.22.6"),sQuery(id+"F4.wireOp",EDGE,"E25.23.0"),sQuery(id+"F4.wireOp",EDGE,"E25.23.1"),sQuery(id+"F4.wireOp",EDGE,"E25.23.3"),sQuery(id+"F4.wireOp",EDGE,"E25.23.4"),sQuery(id+"F4.wireOp",EDGE,"E25.23.5"),sQuery(id+"F4.wireOp",EDGE,"E25.23.6"),sQuery(id+"F4.wireOp",EDGE,"E25.24.0"),sQuery(id+"F4.wireOp",EDGE,"E25.24.1"),sQuery(id+"F4.wireOp",EDGE,"E25.24.3"),sQuery(id+"F4.wireOp",EDGE,"E25.24.4"),sQuery(id+"F4.wireOp",EDGE,"E25.24.5"),sQuery(id+"F4.wireOp",EDGE,"E25.24.6"),sQuery(id+"F4.wireOp",EDGE,"E25.25.0"),sQuery(id+"F4.wireOp",EDGE,"E25.25.1"),sQuery(id+"F4.wireOp",EDGE,"E25.25.3"),sQuery(id+"F4.wireOp",EDGE,"E25.25.4"),sQuery(id+"F4.wireOp",EDGE,"E25.25.5"),sQuery(id+"F4.wireOp",EDGE,"E25.25.6"),sQuery(id+"F4.wireOp",EDGE,"E25.26.0"),sQuery(id+"F4.wireOp",EDGE,"E25.26.1"),sQuery(id+"F4.wireOp",EDGE,"E25.26.3"),sQuery(id+"F4.wireOp",EDGE,"E25.26.4"),sQuery(id+"F4.wireOp",EDGE,"E25.26.5"),sQuery(id+"F4.wireOp",EDGE,"E25.26.6"),sQuery(id+"F4.wireOp",EDGE,"E25.27.0"),sQuery(id+"F4.wireOp",EDGE,"E25.27.1"),sQuery(id+"F4.wireOp",EDGE,"E25.27.3"),sQuery(id+"F4.wireOp",EDGE,"E25.27.4"),sQuery(id+"F4.wireOp",EDGE,"E25.27.5"),sQuery(id+"F4.wireOp",EDGE,"E25.27.6"),sQuery(id+"F4.wireOp",EDGE,"E25.28.0"),sQuery(id+"F4.wireOp",EDGE,"E25.28.1"),sQuery(id+"F4.wireOp",EDGE,"E25.28.3"),sQuery(id+"F4.wireOp",EDGE,"E25.28.4"),sQuery(id+"F4.wireOp",EDGE,"E25.28.5"),sQuery(id+"F4.wireOp",EDGE,"E25.28.6"),sQuery(id+"F4.wireOp",EDGE,"E25.29.0"),sQuery(id+"F4.wireOp",EDGE,"E25.29.1"),sQuery(id+"F4.wireOp",EDGE,"E25.29.3"),sQuery(id+"F4.wireOp",EDGE,"E25.29.4"),sQuery(id+"F4.wireOp",EDGE,"E25.29.5"),sQuery(id+"F4.wireOp",EDGE,"E25.29.6"),sQuery(id+"F4.wireOp",EDGE,"E25.30.0"),sQuery(id+"F4.wireOp",EDGE,"E25.30.1"),sQuery(id+"F4.wireOp",EDGE,"E25.30.3"),sQuery(id+"F4.wireOp",EDGE,"E25.30.4"),sQuery(id+"F4.wireOp",EDGE,"E25.30.5"),sQuery(id+"F4.wireOp",EDGE,"E25.30.6"),sQuery(id+"F4.wireOp",EDGE,"E25.31.0"),sQuery(id+"F4.wireOp",EDGE,"E25.31.1"),sQuery(id+"F4.wireOp",EDGE,"E25.31.3"),sQuery(id+"F4.wireOp",EDGE,"E25.31.4"),sQuery(id+"F4.wireOp",EDGE,"E25.31.5"),sQuery(id+"F4.wireOp",EDGE,"E25.31.6")])],"isStart":false});
            var sketch = newSketch(context, id + "F6", { "sketchPlane" : qUnion([Q0])});
            skCircle(sketch, "E26", {"center": v(0, 0) * mm, "radius": 5 * mm});
            skLineSegment(sketch, "E27.bottom", {"start": v(8.5, 5) * mm, "end": v(11.5, 5) * mm});
            skLineSegment(sketch, "E27.top", {"start": v(8.5, -5) * mm, "end": v(11.5, -5) * mm});
            skLineSegment(sketch, "E27.left", {"start": v(8.5, 5) * mm, "end": v(8.5, -5) * mm});
            skLineSegment(sketch, "E27.right", {"start": v(11.5, 5) * mm, "end": v(11.5, -5) * mm});
            skPoint(sketch, "E27.middle", {"position": v(10, 0) * mm});
            skLineSegment(sketch, "E28.bottom", {"start": v(-11.5, 5) * mm, "end": v(-8.5, 5) * mm});
            skLineSegment(sketch, "E28.top", {"start": v(-11.5, -5) * mm, "end": v(-8.5, -5) * mm});
            skLineSegment(sketch, "E28.left", {"start": v(-11.5, 5) * mm, "end": v(-11.5, -5) * mm});
            skLineSegment(sketch, "E28.right", {"start": v(-8.5, 5) * mm, "end": v(-8.5, -5) * mm});
            skPoint(sketch, "E28.middle", {"position": v(-10, 0) * mm});
            skSolve(sketch);
        }
        {
            var Q0;
            Q0=makeQuery(id+"F6.imprint","IMPRINT",FACE,{"disambiguationData":[TD([[makeQuery(id+"F6.imprint","IMPRINT",EDGE,{"derivedFrom":sQuery(id+"F6.wireOp",EDGE,"E26")}),1.0]])]});
            var Q1;
            Q1=makeQuery(id+"F6.imprint","IMPRINT",FACE,{"disambiguationData":[TD([[makeQuery(id+"F6.imprint","IMPRINT",EDGE,{"derivedFrom":sQuery(id+"F6.wireOp",EDGE,"E28.bottom")}),-1.0]])]});
            var Q2;
            Q2=makeQuery(id+"F6.imprint","IMPRINT",FACE,{"disambiguationData":[TD([[makeQuery(id+"F6.imprint","IMPRINT",EDGE,{"derivedFrom":sQuery(id+"F6.wireOp",EDGE,"E27.bottom")}),-1.0]])]});
            extrude(context, id + "F7", {"entities" : qUnion([Q0, Q1, Q2]), "operationType" : NewBodyOperationType.REMOVE, "oppositeDirection" : true, "depth" : 25 * mm, "offsetDistance" : 25 * mm});
        }
        {
            var Q0;
            Q0=qSketchRegion(id+"F4",true);
            extrude(context, id + "F8", {"entities" : qUnion([Q0]), "depth" : 3 * mm, "offsetDistance" : 25 * mm});
        }
        {
            var Q0;
            Q0=makeQuery(id+"F5.opExtrude","CAP_FACE",FACE,{"disambiguationData":[OSD([sQuery(id+"F4.wireOp",EDGE,"E18.0"),sQuery(id+"F4.wireOp",EDGE,"E19.0"),sQuery(id+"F4.wireOp",EDGE,"E20.0"),sQuery(id+"F4.wireOp",EDGE,"E21.0"),sQuery(id+"F4.wireOp",EDGE,"E23"),sQuery(id+"F4.wireOp",EDGE,"E24"),sQuery(id+"F4.wireOp",EDGE,"E25.1.0"),sQuery(id+"F4.wireOp",EDGE,"E25.1.1"),sQuery(id+"F4.wireOp",EDGE,"E25.1.3"),sQuery(id+"F4.wireOp",EDGE,"E25.1.4"),sQuery(id+"F4.wireOp",EDGE,"E25.1.5"),sQuery(id+"F4.wireOp",EDGE,"E25.1.6"),sQuery(id+"F4.wireOp",EDGE,"E25.2.0"),sQuery(id+"F4.wireOp",EDGE,"E25.2.1"),sQuery(id+"F4.wireOp",EDGE,"E25.2.3"),sQuery(id+"F4.wireOp",EDGE,"E25.2.4"),sQuery(id+"F4.wireOp",EDGE,"E25.2.5"),sQuery(id+"F4.wireOp",EDGE,"E25.2.6"),sQuery(id+"F4.wireOp",EDGE,"E25.3.0"),sQuery(id+"F4.wireOp",EDGE,"E25.3.1"),sQuery(id+"F4.wireOp",EDGE,"E25.3.3"),sQuery(id+"F4.wireOp",EDGE,"E25.3.4"),sQuery(id+"F4.wireOp",EDGE,"E25.3.5"),sQuery(id+"F4.wireOp",EDGE,"E25.3.6"),sQuery(id+"F4.wireOp",EDGE,"E25.4.0"),sQuery(id+"F4.wireOp",EDGE,"E25.4.1"),sQuery(id+"F4.wireOp",EDGE,"E25.4.3"),sQuery(id+"F4.wireOp",EDGE,"E25.4.4"),sQuery(id+"F4.wireOp",EDGE,"E25.4.5"),sQuery(id+"F4.wireOp",EDGE,"E25.4.6"),sQuery(id+"F4.wireOp",EDGE,"E25.5.0"),sQuery(id+"F4.wireOp",EDGE,"E25.5.1"),sQuery(id+"F4.wireOp",EDGE,"E25.5.3"),sQuery(id+"F4.wireOp",EDGE,"E25.5.4"),sQuery(id+"F4.wireOp",EDGE,"E25.5.5"),sQuery(id+"F4.wireOp",EDGE,"E25.5.6"),sQuery(id+"F4.wireOp",EDGE,"E25.6.0"),sQuery(id+"F4.wireOp",EDGE,"E25.6.1"),sQuery(id+"F4.wireOp",EDGE,"E25.6.3"),sQuery(id+"F4.wireOp",EDGE,"E25.6.4"),sQuery(id+"F4.wireOp",EDGE,"E25.6.5"),sQuery(id+"F4.wireOp",EDGE,"E25.6.6"),sQuery(id+"F4.wireOp",EDGE,"E25.7.0"),sQuery(id+"F4.wireOp",EDGE,"E25.7.1"),sQuery(id+"F4.wireOp",EDGE,"E25.7.3"),sQuery(id+"F4.wireOp",EDGE,"E25.7.4"),sQuery(id+"F4.wireOp",EDGE,"E25.7.5"),sQuery(id+"F4.wireOp",EDGE,"E25.7.6"),sQuery(id+"F4.wireOp",EDGE,"E25.8.0"),sQuery(id+"F4.wireOp",EDGE,"E25.8.1"),sQuery(id+"F4.wireOp",EDGE,"E25.8.3"),sQuery(id+"F4.wireOp",EDGE,"E25.8.4"),sQuery(id+"F4.wireOp",EDGE,"E25.8.5"),sQuery(id+"F4.wireOp",EDGE,"E25.8.6"),sQuery(id+"F4.wireOp",EDGE,"E25.9.0"),sQuery(id+"F4.wireOp",EDGE,"E25.9.1"),sQuery(id+"F4.wireOp",EDGE,"E25.9.3"),sQuery(id+"F4.wireOp",EDGE,"E25.9.4"),sQuery(id+"F4.wireOp",EDGE,"E25.9.5"),sQuery(id+"F4.wireOp",EDGE,"E25.9.6"),sQuery(id+"F4.wireOp",EDGE,"E25.10.0"),sQuery(id+"F4.wireOp",EDGE,"E25.10.1"),sQuery(id+"F4.wireOp",EDGE,"E25.10.3"),sQuery(id+"F4.wireOp",EDGE,"E25.10.4"),sQuery(id+"F4.wireOp",EDGE,"E25.10.5"),sQuery(id+"F4.wireOp",EDGE,"E25.10.6"),sQuery(id+"F4.wireOp",EDGE,"E25.11.0"),sQuery(id+"F4.wireOp",EDGE,"E25.11.1"),sQuery(id+"F4.wireOp",EDGE,"E25.11.3"),sQuery(id+"F4.wireOp",EDGE,"E25.11.4"),sQuery(id+"F4.wireOp",EDGE,"E25.11.5"),sQuery(id+"F4.wireOp",EDGE,"E25.11.6"),sQuery(id+"F4.wireOp",EDGE,"E25.12.0"),sQuery(id+"F4.wireOp",EDGE,"E25.12.1"),sQuery(id+"F4.wireOp",EDGE,"E25.12.3"),sQuery(id+"F4.wireOp",EDGE,"E25.12.4"),sQuery(id+"F4.wireOp",EDGE,"E25.12.5"),sQuery(id+"F4.wireOp",EDGE,"E25.12.6"),sQuery(id+"F4.wireOp",EDGE,"E25.13.0"),sQuery(id+"F4.wireOp",EDGE,"E25.13.1"),sQuery(id+"F4.wireOp",EDGE,"E25.13.3"),sQuery(id+"F4.wireOp",EDGE,"E25.13.4"),sQuery(id+"F4.wireOp",EDGE,"E25.13.5"),sQuery(id+"F4.wireOp",EDGE,"E25.13.6"),sQuery(id+"F4.wireOp",EDGE,"E25.14.0"),sQuery(id+"F4.wireOp",EDGE,"E25.14.1"),sQuery(id+"F4.wireOp",EDGE,"E25.14.3"),sQuery(id+"F4.wireOp",EDGE,"E25.14.4"),sQuery(id+"F4.wireOp",EDGE,"E25.14.5"),sQuery(id+"F4.wireOp",EDGE,"E25.14.6"),sQuery(id+"F4.wireOp",EDGE,"E25.15.0"),sQuery(id+"F4.wireOp",EDGE,"E25.15.1"),sQuery(id+"F4.wireOp",EDGE,"E25.15.3"),sQuery(id+"F4.wireOp",EDGE,"E25.15.4"),sQuery(id+"F4.wireOp",EDGE,"E25.15.5"),sQuery(id+"F4.wireOp",EDGE,"E25.15.6"),sQuery(id+"F4.wireOp",EDGE,"E25.16.0"),sQuery(id+"F4.wireOp",EDGE,"E25.16.1"),sQuery(id+"F4.wireOp",EDGE,"E25.16.3"),sQuery(id+"F4.wireOp",EDGE,"E25.16.4"),sQuery(id+"F4.wireOp",EDGE,"E25.16.5"),sQuery(id+"F4.wireOp",EDGE,"E25.16.6"),sQuery(id+"F4.wireOp",EDGE,"E25.17.0"),sQuery(id+"F4.wireOp",EDGE,"E25.17.1"),sQuery(id+"F4.wireOp",EDGE,"E25.17.3"),sQuery(id+"F4.wireOp",EDGE,"E25.17.4"),sQuery(id+"F4.wireOp",EDGE,"E25.17.5"),sQuery(id+"F4.wireOp",EDGE,"E25.17.6"),sQuery(id+"F4.wireOp",EDGE,"E25.18.0"),sQuery(id+"F4.wireOp",EDGE,"E25.18.1"),sQuery(id+"F4.wireOp",EDGE,"E25.18.3"),sQuery(id+"F4.wireOp",EDGE,"E25.18.4"),sQuery(id+"F4.wireOp",EDGE,"E25.18.5"),sQuery(id+"F4.wireOp",EDGE,"E25.18.6"),sQuery(id+"F4.wireOp",EDGE,"E25.19.0"),sQuery(id+"F4.wireOp",EDGE,"E25.19.1"),sQuery(id+"F4.wireOp",EDGE,"E25.19.3"),sQuery(id+"F4.wireOp",EDGE,"E25.19.4"),sQuery(id+"F4.wireOp",EDGE,"E25.19.5"),sQuery(id+"F4.wireOp",EDGE,"E25.19.6"),sQuery(id+"F4.wireOp",EDGE,"E25.20.0"),sQuery(id+"F4.wireOp",EDGE,"E25.20.1"),sQuery(id+"F4.wireOp",EDGE,"E25.20.3"),sQuery(id+"F4.wireOp",EDGE,"E25.20.4"),sQuery(id+"F4.wireOp",EDGE,"E25.20.5"),sQuery(id+"F4.wireOp",EDGE,"E25.20.6"),sQuery(id+"F4.wireOp",EDGE,"E25.21.0"),sQuery(id+"F4.wireOp",EDGE,"E25.21.1"),sQuery(id+"F4.wireOp",EDGE,"E25.21.3"),sQuery(id+"F4.wireOp",EDGE,"E25.21.4"),sQuery(id+"F4.wireOp",EDGE,"E25.21.5"),sQuery(id+"F4.wireOp",EDGE,"E25.21.6"),sQuery(id+"F4.wireOp",EDGE,"E25.22.0"),sQuery(id+"F4.wireOp",EDGE,"E25.22.1"),sQuery(id+"F4.wireOp",EDGE,"E25.22.3"),sQuery(id+"F4.wireOp",EDGE,"E25.22.4"),sQuery(id+"F4.wireOp",EDGE,"E25.22.5"),sQuery(id+"F4.wireOp",EDGE,"E25.22.6"),sQuery(id+"F4.wireOp",EDGE,"E25.23.0"),sQuery(id+"F4.wireOp",EDGE,"E25.23.1"),sQuery(id+"F4.wireOp",EDGE,"E25.23.3"),sQuery(id+"F4.wireOp",EDGE,"E25.23.4"),sQuery(id+"F4.wireOp",EDGE,"E25.23.5"),sQuery(id+"F4.wireOp",EDGE,"E25.23.6"),sQuery(id+"F4.wireOp",EDGE,"E25.24.0"),sQuery(id+"F4.wireOp",EDGE,"E25.24.1"),sQuery(id+"F4.wireOp",EDGE,"E25.24.3"),sQuery(id+"F4.wireOp",EDGE,"E25.24.4"),sQuery(id+"F4.wireOp",EDGE,"E25.24.5"),sQuery(id+"F4.wireOp",EDGE,"E25.24.6"),sQuery(id+"F4.wireOp",EDGE,"E25.25.0"),sQuery(id+"F4.wireOp",EDGE,"E25.25.1"),sQuery(id+"F4.wireOp",EDGE,"E25.25.3"),sQuery(id+"F4.wireOp",EDGE,"E25.25.4"),sQuery(id+"F4.wireOp",EDGE,"E25.25.5"),sQuery(id+"F4.wireOp",EDGE,"E25.25.6"),sQuery(id+"F4.wireOp",EDGE,"E25.26.0"),sQuery(id+"F4.wireOp",EDGE,"E25.26.1"),sQuery(id+"F4.wireOp",EDGE,"E25.26.3"),sQuery(id+"F4.wireOp",EDGE,"E25.26.4"),sQuery(id+"F4.wireOp",EDGE,"E25.26.5"),sQuery(id+"F4.wireOp",EDGE,"E25.26.6"),sQuery(id+"F4.wireOp",EDGE,"E25.27.0"),sQuery(id+"F4.wireOp",EDGE,"E25.27.1"),sQuery(id+"F4.wireOp",EDGE,"E25.27.3"),sQuery(id+"F4.wireOp",EDGE,"E25.27.4"),sQuery(id+"F4.wireOp",EDGE,"E25.27.5"),sQuery(id+"F4.wireOp",EDGE,"E25.27.6"),sQuery(id+"F4.wireOp",EDGE,"E25.28.0"),sQuery(id+"F4.wireOp",EDGE,"E25.28.1"),sQuery(id+"F4.wireOp",EDGE,"E25.28.3"),sQuery(id+"F4.wireOp",EDGE,"E25.28.4"),sQuery(id+"F4.wireOp",EDGE,"E25.28.5"),sQuery(id+"F4.wireOp",EDGE,"E25.28.6"),sQuery(id+"F4.wireOp",EDGE,"E25.29.0"),sQuery(id+"F4.wireOp",EDGE,"E25.29.1"),sQuery(id+"F4.wireOp",EDGE,"E25.29.3"),sQuery(id+"F4.wireOp",EDGE,"E25.29.4"),sQuery(id+"F4.wireOp",EDGE,"E25.29.5"),sQuery(id+"F4.wireOp",EDGE,"E25.29.6"),sQuery(id+"F4.wireOp",EDGE,"E25.30.0"),sQuery(id+"F4.wireOp",EDGE,"E25.30.1"),sQuery(id+"F4.wireOp",EDGE,"E25.30.3"),sQuery(id+"F4.wireOp",EDGE,"E25.30.4"),sQuery(id+"F4.wireOp",EDGE,"E25.30.5"),sQuery(id+"F4.wireOp",EDGE,"E25.30.6"),sQuery(id+"F4.wireOp",EDGE,"E25.31.0"),sQuery(id+"F4.wireOp",EDGE,"E25.31.1"),sQuery(id+"F4.wireOp",EDGE,"E25.31.3"),sQuery(id+"F4.wireOp",EDGE,"E25.31.4"),sQuery(id+"F4.wireOp",EDGE,"E25.31.5"),sQuery(id+"F4.wireOp",EDGE,"E25.31.6")])],"isStart":false});
            var sketch = newSketch(context, id + "F9", { "sketchPlane" : qUnion([Q0])});
            skLineSegment(sketch, "E29.bottom", {"start": v(4.5, 1.5) * mm, "end": v(-4.5, 1.5) * mm});
            skLineSegment(sketch, "E29.top", {"start": v(4.5, -1.5) * mm, "end": v(-4.5, -1.5) * mm});
            skLineSegment(sketch, "E29.left", {"start": v(4.5, 1.5) * mm, "end": v(4.5, -1.5) * mm});
            skLineSegment(sketch, "E29.right", {"start": v(-4.5, 1.5) * mm, "end": v(-4.5, -1.5) * mm});
            skPoint(sketch, "E29.middle", {"position": v(0, 0) * mm});
            skLineSegment(sketch, "E30.bottom", {"start": v(1.5, 4.5) * mm, "end": v(-1.5, 4.5) * mm});
            skLineSegment(sketch, "E30.top", {"start": v(1.5, -4.5) * mm, "end": v(-1.5, -4.5) * mm});
            skLineSegment(sketch, "E30.left", {"start": v(1.5, 4.5) * mm, "end": v(1.5, -4.5) * mm});
            skLineSegment(sketch, "E30.right", {"start": v(-1.5, 4.5) * mm, "end": v(-1.5, -4.5) * mm});
            skSolve(sketch);
        }
        {
            var Q0;
            Q0=qSketchRegion(id+"F9",true);
            extrude(context, id + "F10", {"entities" : qUnion([Q0]), "operationType" : NewBodyOperationType.REMOVE, "oppositeDirection" : true, "depth" : 25 * mm, "offsetDistance" : 25 * mm});
        }
    });
